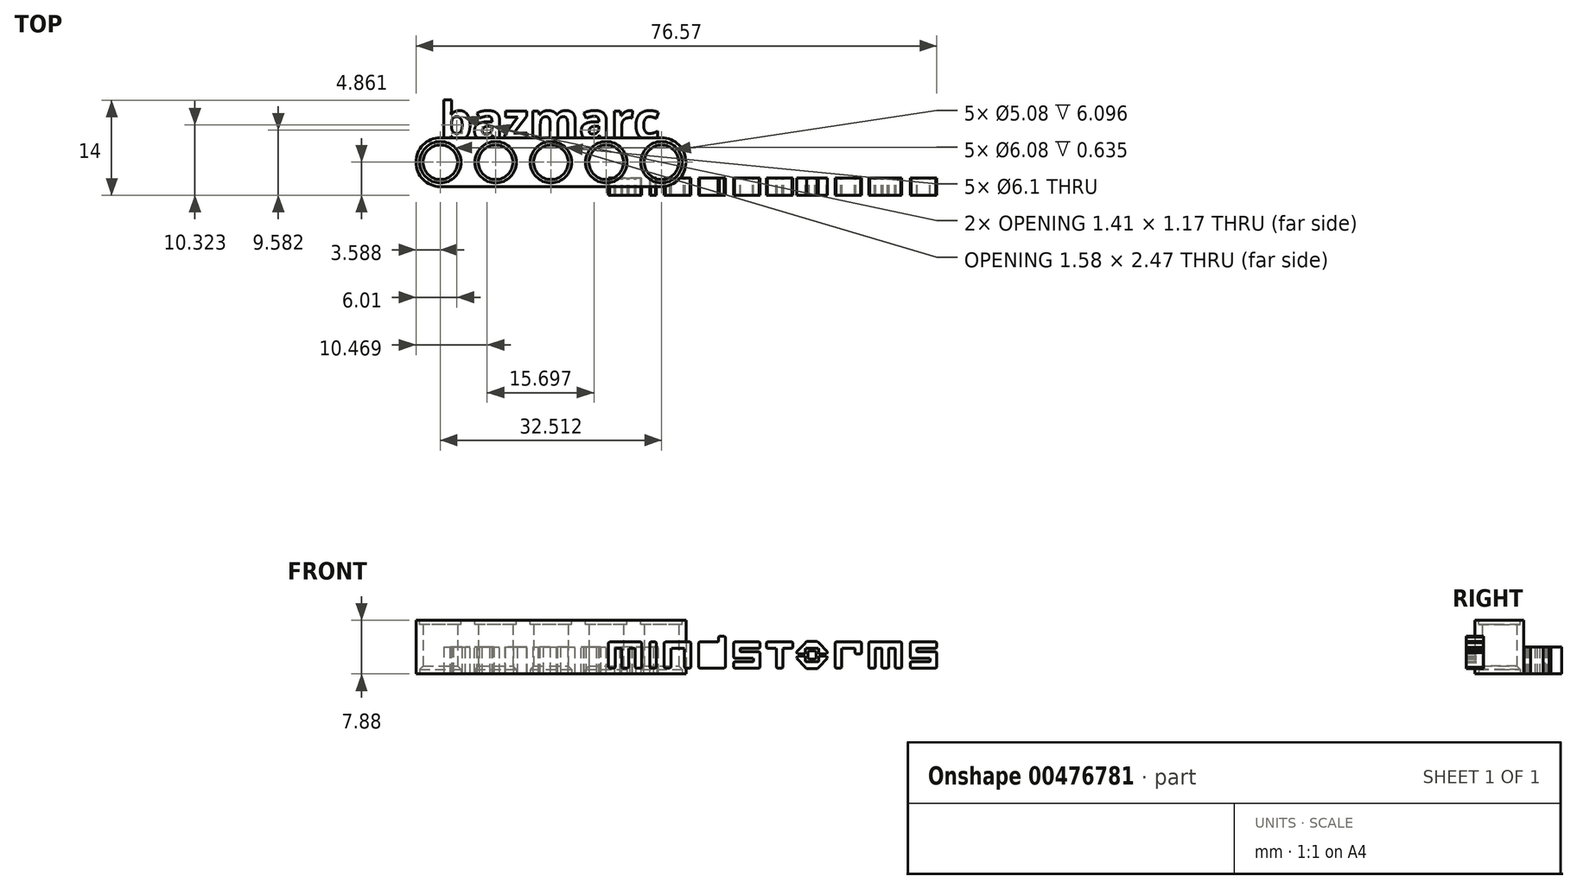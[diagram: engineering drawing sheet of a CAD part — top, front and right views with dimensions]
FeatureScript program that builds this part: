
annotation { "Feature Type Name" : "Feature", "Feature Type Description" : "" }
export const myFeature = defineFeature(function(context is Context, id is Id, definition is map)
    precondition{}
    {
        {
            var Q0;
            Q0=qCreatedBy(makeId("Top.planeOp"),FACE);
            var sketch = newSketch(context, id + "F0", { "sketchPlane" : qUnion([Q0])});
            skCircle(sketch, "E0", {"center": v(-60.84, 14.37) * mm, "radius": 3.6 * mm});
            skCircle(sketch, "E1.1.0.0", {"center": v(-52.71, 14.37) * mm, "radius": 3.6 * mm});
            skCircle(sketch, "E1.2.0.0", {"center": v(-44.59, 14.37) * mm, "radius": 3.6 * mm});
            skCircle(sketch, "E1.3.0.0", {"center": v(-36.46, 14.37) * mm, "radius": 3.6 * mm});
            skLineSegment(sketch, "E1.direction1", {"start": v(-60.84, 14.37) * mm, "end": v(-52.71, 14.37) * mm, "construction": true});
            skCircle(sketch, "E2.0.4.0", {"center": v(-28.33, 14.37) * mm, "radius": 3.6 * mm});
            skLineSegment(sketch, "E3.left", {"start": v(-60.84, 14.37) * mm, "end": v(-60.84, 14.37) * mm});
            skLineSegment(sketch, "E3.right", {"start": v(-28.33, 14.37) * mm, "end": v(-28.33, 14.37) * mm});
            skLineSegment(sketch, "E4.bottom", {"start": v(-60.84, 17.96) * mm, "end": v(-28.33, 17.96) * mm});
            skLineSegment(sketch, "E4.top", {"start": v(-60.84, 10.78) * mm, "end": v(-28.33, 10.78) * mm});
            skCircle(sketch, "E5", {"center": v(-60.84, 14.37) * mm, "radius": 3.05 * mm});
            skCircle(sketch, "E6.1.0.0", {"center": v(-52.71, 14.37) * mm, "radius": 3.05 * mm});
            skCircle(sketch, "E6.2.0.0", {"center": v(-44.59, 14.37) * mm, "radius": 3.05 * mm});
            skCircle(sketch, "E6.3.0.0", {"center": v(-36.46, 14.37) * mm, "radius": 3.05 * mm});
            skCircle(sketch, "E6.4.0.0", {"center": v(-28.33, 14.37) * mm, "radius": 3.05 * mm});
            skCircle(sketch, "E7", {"center": v(-60.84, 14.37) * mm, "radius": 2.54 * mm});
            skCircle(sketch, "E8.1.0.0", {"center": v(-52.71, 14.37) * mm, "radius": 2.54 * mm});
            skCircle(sketch, "E8.2.0.0", {"center": v(-44.59, 14.37) * mm, "radius": 2.54 * mm});
            skCircle(sketch, "E8.3.0.0", {"center": v(-36.46, 14.37) * mm, "radius": 2.54 * mm});
            skCircle(sketch, "E8.4.0.0", {"center": v(-28.33, 14.37) * mm, "radius": 2.54 * mm});
            skSolve(sketch);
        }
        {
            var Q0;
            Q0=makeQuery(id+"F0.imprint","IMPRINT",FACE,{"disambiguationData":[TD([[makeQuery(id+"F0.imprint","IMPRINT",EDGE,{"derivedFrom":sQuery(id+"F0.wireOp",EDGE,"E6.2.0.0")}),1.0]])]});
            var Q1;
            {var subQ0=sQuery(id+"F0.wireOp",EDGE,"E4.bottom");var subQ1=sQuery(id+"F0.wireOp",EDGE,"E0");var subQ2=makeQuery(id+"F0.imprint","INTERSECT",VERTEX,{"derivedFrom":[subQ1,subQ0]});Q1=makeQuery(id+"F0.imprint","IMPRINT",FACE,{"disambiguationData":[TD([[makeQuery(id+"F0.imprint","IMPRINT",EDGE,{"disambiguationData":[TD([[subQ2,1.0]])],"derivedFrom":subQ1}),-1.0]])]});}
            var Q2;
            {var subQ0=sQuery(id+"F0.wireOp",EDGE,"E4.bottom");var subQ1=sQuery(id+"F0.wireOp",EDGE,"E1.1.0.0");var subQ2=makeQuery(id+"F0.imprint","INTERSECT",VERTEX,{"derivedFrom":[subQ1,subQ0]});Q2=makeQuery(id+"F0.imprint","IMPRINT",FACE,{"disambiguationData":[TD([[makeQuery(id+"F0.imprint","IMPRINT",EDGE,{"disambiguationData":[TD([[subQ2,1.0]])],"derivedFrom":subQ1}),-1.0]])]});}
            var Q3;
            Q3=makeQuery(id+"F0.imprint","IMPRINT",FACE,{"disambiguationData":[TD([[makeQuery(id+"F0.imprint","IMPRINT",EDGE,{"derivedFrom":sQuery(id+"F0.wireOp",EDGE,"E6.2.0.0")}),-1.0]])]});
            var Q4;
            Q4=makeQuery(id+"F0.imprint","IMPRINT",FACE,{"disambiguationData":[TD([[makeQuery(id+"F0.imprint","IMPRINT",EDGE,{"derivedFrom":sQuery(id+"F0.wireOp",EDGE,"E6.1.0.0")}),-1.0]])]});
            var Q5;
            Q5=makeQuery(id+"F0.imprint","IMPRINT",FACE,{"disambiguationData":[TD([[makeQuery(id+"F0.imprint","IMPRINT",EDGE,{"derivedFrom":sQuery(id+"F0.wireOp",EDGE,"E6.3.0.0")}),-1.0]])]});
            var Q6;
            Q6=makeQuery(id+"F0.imprint","IMPRINT",FACE,{"disambiguationData":[TD([[makeQuery(id+"F0.imprint","IMPRINT",EDGE,{"derivedFrom":sQuery(id+"F0.wireOp",EDGE,"E6.3.0.0")}),1.0]])]});
            var Q7;
            {var subQ0=sQuery(id+"F0.wireOp",EDGE,"E4.bottom");var subQ1=sQuery(id+"F0.wireOp",EDGE,"E1.3.0.0");var subQ2=makeQuery(id+"F0.imprint","INTERSECT",VERTEX,{"derivedFrom":[subQ1,subQ0]});Q7=makeQuery(id+"F0.imprint","IMPRINT",FACE,{"disambiguationData":[TD([[makeQuery(id+"F0.imprint","IMPRINT",EDGE,{"disambiguationData":[TD([[subQ2,1.0]])],"derivedFrom":subQ1}),-1.0]])]});}
            var Q8;
            Q8=makeQuery(id+"F0.imprint","IMPRINT",FACE,{"disambiguationData":[TD([[makeQuery(id+"F0.imprint","IMPRINT",EDGE,{"derivedFrom":sQuery(id+"F0.wireOp",EDGE,"E6.4.0.0")}),-1.0]])]});
            var Q9;
            Q9=makeQuery(id+"F0.imprint","IMPRINT",FACE,{"disambiguationData":[TD([[makeQuery(id+"F0.imprint","IMPRINT",EDGE,{"derivedFrom":sQuery(id+"F0.wireOp",EDGE,"E6.1.0.0")}),1.0]])]});
            var Q10;
            {var subQ0=sQuery(id+"F0.wireOp",EDGE,"E4.bottom");var subQ1=sQuery(id+"F0.wireOp",EDGE,"E1.2.0.0");var subQ2=makeQuery(id+"F0.imprint","INTERSECT",VERTEX,{"derivedFrom":[subQ1,subQ0]});Q10=makeQuery(id+"F0.imprint","IMPRINT",FACE,{"disambiguationData":[TD([[makeQuery(id+"F0.imprint","IMPRINT",EDGE,{"disambiguationData":[TD([[subQ2,1.0]])],"derivedFrom":subQ1}),-1.0]])]});}
            var Q11;
            Q11=makeQuery(id+"F0.imprint","IMPRINT",FACE,{"disambiguationData":[TD([[makeQuery(id+"F0.imprint","IMPRINT",EDGE,{"derivedFrom":sQuery(id+"F0.wireOp",EDGE,"E6.4.0.0")}),1.0]])]});
            var Q12;
            Q12=makeQuery(id+"F0.imprint","IMPRINT",FACE,{"disambiguationData":[TD([[makeQuery(id+"F0.imprint","IMPRINT",EDGE,{"derivedFrom":sQuery(id+"F0.wireOp",EDGE,"E5")}),-1.0]])]});
            var Q13;
            Q13=makeQuery(id+"F0.imprint","IMPRINT",FACE,{"disambiguationData":[TD([[makeQuery(id+"F0.imprint","IMPRINT",EDGE,{"derivedFrom":sQuery(id+"F0.wireOp",EDGE,"E5")}),1.0]])]});
            extrude(context, id + "F1", {"entities" : qUnion([Q0, Q1, Q2, Q3, Q4, Q5, Q6, Q7, Q8, Q9, Q10, Q11, Q12, Q13]), "endBound" : BoundingType.SYMMETRIC, "depth" : 7.87 * mm});
        }
        {
            var Q0;
            Q0=makeQuery(id+"F1.opExtrude","CAP_FACE",FACE,{"disambiguationData":[OSD([sQuery(id+"F0.wireOp",EDGE,"E0"),sQuery(id+"F0.wireOp",EDGE,"E2.0.4.0"),sQuery(id+"F0.wireOp",EDGE,"E4.bottom"),sQuery(id+"F0.wireOp",EDGE,"E4.top"),sQuery(id+"F0.wireOp",EDGE,"E7"),sQuery(id+"F0.wireOp",EDGE,"E8.1.0.0"),sQuery(id+"F0.wireOp",EDGE,"E8.2.0.0"),sQuery(id+"F0.wireOp",EDGE,"E8.3.0.0"),sQuery(id+"F0.wireOp",EDGE,"E8.4.0.0")])],"isStart":false});
            var sketch = newSketch(context, id + "F2", { "sketchPlane" : qUnion([Q0])});
            skCircle(sketch, "E9", {"center": v(-28.33, 14.37) * mm, "radius": 3.04 * mm});
            skCircle(sketch, "E10.1.0.0", {"center": v(-36.46, 14.37) * mm, "radius": 3.04 * mm});
            skCircle(sketch, "E10.2.0.0", {"center": v(-44.59, 14.37) * mm, "radius": 3.04 * mm});
            skCircle(sketch, "E10.3.0.0", {"center": v(-52.71, 14.37) * mm, "radius": 3.04 * mm});
            skCircle(sketch, "E10.4.0.0", {"center": v(-60.84, 14.37) * mm, "radius": 3.04 * mm});
            skLineSegment(sketch, "E10.direction1", {"start": v(-28.33, 14.37) * mm, "end": v(-36.46, 14.37) * mm, "construction": true});
            skSolve(sketch);
        }
        {
            var Q0;
            Q0=qSketchRegion(id+"F2",true);
            extrude(context, id + "F3", {"entities" : qUnion([Q0]), "operationType" : NewBodyOperationType.REMOVE, "oppositeDirection" : true, "depth" : 0.64 * mm});
        }
        {
            var Q0;
            Q0=makeQuery(id+"F1.opExtrude","CAP_FACE",FACE,{"disambiguationData":[OSD([sQuery(id+"F0.wireOp",EDGE,"E0"),sQuery(id+"F0.wireOp",EDGE,"E2.0.4.0"),sQuery(id+"F0.wireOp",EDGE,"E4.bottom"),sQuery(id+"F0.wireOp",EDGE,"E4.top"),sQuery(id+"F0.wireOp",EDGE,"E7"),sQuery(id+"F0.wireOp",EDGE,"E8.1.0.0"),sQuery(id+"F0.wireOp",EDGE,"E8.2.0.0"),sQuery(id+"F0.wireOp",EDGE,"E8.3.0.0"),sQuery(id+"F0.wireOp",EDGE,"E8.4.0.0")])],"isStart":true});
            var sketch = newSketch(context, id + "F4", { "sketchPlane" : qUnion([Q0])});
            skCircle(sketch, "E11", {"center": v(-60.84, -14.37) * mm, "radius": 3.05 * mm});
            skCircle(sketch, "E12.1.0.0", {"center": v(-52.71, -14.37) * mm, "radius": 3.05 * mm});
            skCircle(sketch, "E12.2.0.0", {"center": v(-44.59, -14.37) * mm, "radius": 3.05 * mm});
            skCircle(sketch, "E12.3.0.0", {"center": v(-36.46, -14.37) * mm, "radius": 3.05 * mm});
            skCircle(sketch, "E12.4.0.0", {"center": v(-28.33, -14.37) * mm, "radius": 3.05 * mm});
            skLineSegment(sketch, "E12.direction1", {"start": v(-60.84, -14.37) * mm, "end": v(-52.71, -14.37) * mm, "construction": true});
            skSolve(sketch);
        }
        {
            var Q0;
            Q0=qSketchRegion(id+"F4",true);
            extrude(context, id + "F5", {"entities" : qUnion([Q0]), "operationType" : NewBodyOperationType.REMOVE, "oppositeDirection" : true, "depth" : 0.64 * mm});
        }
        {
            var Q0;
            Q0=qCreatedBy(makeId("Top.planeOp"),FACE);
            var sketch = newSketch(context, id + "F6", { "sketchPlane" : qUnion([Q0])});
            skText(sketch, "E13", { "text": "bazmarc", "fontName": "OpenSans-Bold.ttf"});
            const initialGuessF6  = {"E13": [-0.06093, 0.01776, 1, 0, 0.00545]};
            skSetInitialGuess(sketch, initialGuessF6);
            skSolve(sketch);
        }
        {
            var Q0;
            Q0=qSketchRegion(id+"F6",true);
            extrude(context, id + "F7", {"entities" : qUnion([Q0]), "operationType" : NewBodyOperationType.ADD, "oppositeDirection" : true, "depth" : 3.94 * mm});
        }
        {
            var Q0;
            Q0=makeQuery(id+"F5.boolean.opBoolean","INTERSECT",EDGE,{"derivedFrom":[makeQuery(id+"F1.opExtrude","SWEPT_FACE",FACE,{"disambiguationData":[OSD([sQuery(id+"F0.wireOp",EDGE,"E8.3.0.0")])]}),makeQuery(id+"F5.opExtrude","CAP_FACE",FACE,{"disambiguationData":[OSD([sQuery(id+"F4.wireOp",EDGE,"E12.3.0.0")])],"isStart":false})]});
            chamfer(context, id + "F8", {"entities" : qUnion([Q0]), "chamferType" : ChamferType.OFFSET_ANGLE, "width" : 0.5 * mm, "oppositeDirection" : false, "angle" : 45 * degree});
        }
        {
            var Q0;
            Q0=makeQuery(id+"F5.boolean.opBoolean","INTERSECT",EDGE,{"derivedFrom":[makeQuery(id+"F1.opExtrude","SWEPT_FACE",FACE,{"disambiguationData":[OSD([sQuery(id+"F0.wireOp",EDGE,"E8.2.0.0")])]}),makeQuery(id+"F5.opExtrude","CAP_FACE",FACE,{"disambiguationData":[OSD([sQuery(id+"F4.wireOp",EDGE,"E12.2.0.0")])],"isStart":false})]});
            var Q1;
            Q1=makeQuery(id+"F5.boolean.opBoolean","INTERSECT",EDGE,{"derivedFrom":[makeQuery(id+"F1.opExtrude","SWEPT_FACE",FACE,{"disambiguationData":[OSD([sQuery(id+"F0.wireOp",EDGE,"E8.1.0.0")])]}),makeQuery(id+"F5.opExtrude","CAP_FACE",FACE,{"disambiguationData":[OSD([sQuery(id+"F4.wireOp",EDGE,"E12.1.0.0")])],"isStart":false})]});
            var Q2;
            Q2=makeQuery(id+"F5.boolean.opBoolean","INTERSECT",EDGE,{"derivedFrom":[makeQuery(id+"F1.opExtrude","SWEPT_FACE",FACE,{"disambiguationData":[OSD([sQuery(id+"F0.wireOp",EDGE,"E7")])]}),makeQuery(id+"F5.opExtrude","CAP_FACE",FACE,{"disambiguationData":[OSD([sQuery(id+"F4.wireOp",EDGE,"E11")])],"isStart":false})]});
            var Q3;
            Q3=makeQuery(id+"F5.boolean.opBoolean","INTERSECT",EDGE,{"derivedFrom":[makeQuery(id+"F1.opExtrude","SWEPT_FACE",FACE,{"disambiguationData":[OSD([sQuery(id+"F0.wireOp",EDGE,"E8.4.0.0")])]}),makeQuery(id+"F5.opExtrude","CAP_FACE",FACE,{"disambiguationData":[OSD([sQuery(id+"F4.wireOp",EDGE,"E12.4.0.0")])],"isStart":false})]});
            chamfer(context, id + "F9", {"entities" : qUnion([Q0, Q1, Q2, Q3]), "chamferType" : ChamferType.OFFSET_ANGLE, "width" : 0.5 * mm, "oppositeDirection" : false, "angle" : 45 * degree});
        }
        {
            var Q0;
            Q0=makeQuery(id+"F1.opExtrude","SWEPT_FACE",FACE,{"disambiguationData":[OSD([sQuery(id+"F0.wireOp",EDGE,"E4.top")])]});
            var sketch = newSketch(context, id + "F10", { "sketchPlane" : qUnion([Q0])});
            skLineSegment(sketch, "E14", {"start": v(3.4, -0.27) * mm, "end": v(3.94, -0.27) * mm});
            skLineSegment(sketch, "E15", {"start": v(3.94, -0.27) * mm, "end": v(3.96, -0.27) * mm});
            skLineSegment(sketch, "E16", {"start": v(3.96, -0.27) * mm, "end": v(4.03, -0.42) * mm});
            skLineSegment(sketch, "E17", {"start": v(4.03, -0.42) * mm, "end": v(4.02, -0.43) * mm});
            skLineSegment(sketch, "E18", {"start": v(4.02, -0.43) * mm, "end": v(3.38, -1.1) * mm});
            skLineSegment(sketch, "E19", {"start": v(3.38, -1.1) * mm, "end": v(3.36, -1.13) * mm});
            skLineSegment(sketch, "E20", {"start": v(3.36, -1.13) * mm, "end": v(3.28, -1.2) * mm});
            skLineSegment(sketch, "E21", {"start": v(3.28, -1.2) * mm, "end": v(3.26, -1.2) * mm});
            skLineSegment(sketch, "E22", {"start": v(3.26, -1.2) * mm, "end": v(2.53, -1.2) * mm});
            skLineSegment(sketch, "E23", {"start": v(2.53, -1.2) * mm, "end": v(2.5, -1.2) * mm});
            skLineSegment(sketch, "E24", {"start": v(2.5, -1.2) * mm, "end": v(2.41, -1.12) * mm});
            skLineSegment(sketch, "E25", {"start": v(2.41, -1.12) * mm, "end": v(2.39, -1.09) * mm});
            skLineSegment(sketch, "E26", {"start": v(2.39, -1.09) * mm, "end": v(1.77, -0.43) * mm});
            skLineSegment(sketch, "E27", {"start": v(1.77, -0.43) * mm, "end": v(1.75, -0.42) * mm});
            skLineSegment(sketch, "E28", {"start": v(1.75, -0.42) * mm, "end": v(1.82, -0.27) * mm});
            skLineSegment(sketch, "E29", {"start": v(1.82, -0.27) * mm, "end": v(1.84, -0.27) * mm});
            skLineSegment(sketch, "E30", {"start": v(1.84, -0.27) * mm, "end": v(2.4, -0.27) * mm});
            skLineSegment(sketch, "E31", {"start": v(2.4, -0.27) * mm, "end": v(2.4, -0.64) * mm});
            skLineSegment(sketch, "E32", {"start": v(2.4, -0.64) * mm, "end": v(2.4, -0.64) * mm});
            skLineSegment(sketch, "E33", {"start": v(2.4, -0.64) * mm, "end": v(2.43, -0.68) * mm});
            skLineSegment(sketch, "E34", {"start": v(2.43, -0.68) * mm, "end": v(2.44, -0.68) * mm});
            skLineSegment(sketch, "E35", {"start": v(2.44, -0.68) * mm, "end": v(3.34, -0.68) * mm});
            skLineSegment(sketch, "E36", {"start": v(3.34, -0.68) * mm, "end": v(3.35, -0.68) * mm});
            skLineSegment(sketch, "E37", {"start": v(3.35, -0.68) * mm, "end": v(3.4, -0.65) * mm});
            skLineSegment(sketch, "E38", {"start": v(3.4, -0.65) * mm, "end": v(3.4, -0.64) * mm});
            skLineSegment(sketch, "E39", {"start": v(3.4, -0.64) * mm, "end": v(3.4, -0.27) * mm});
            skLineSegment(sketch, "E40", {"start": v(3.4, -0.12) * mm, "end": v(3.94, -0.12) * mm});
            skLineSegment(sketch, "E41", {"start": v(3.94, -0.12) * mm, "end": v(3.96, -0.12) * mm});
            skLineSegment(sketch, "E42", {"start": v(3.96, -0.12) * mm, "end": v(4.03, 0.03) * mm});
            skLineSegment(sketch, "E43", {"start": v(4.03, 0.03) * mm, "end": v(4.02, 0.04) * mm});
            skLineSegment(sketch, "E44", {"start": v(4.02, 0.04) * mm, "end": v(3.38, 0.7) * mm});
            skLineSegment(sketch, "E45", {"start": v(3.38, 0.7) * mm, "end": v(3.36, 0.73) * mm});
            skLineSegment(sketch, "E46", {"start": v(3.36, 0.73) * mm, "end": v(3.27, 0.8) * mm});
            skLineSegment(sketch, "E47", {"start": v(3.27, 0.8) * mm, "end": v(3.26, 0.8) * mm});
            skLineSegment(sketch, "E48", {"start": v(3.26, 0.8) * mm, "end": v(2.53, 0.8) * mm});
            skLineSegment(sketch, "E49", {"start": v(2.53, 0.8) * mm, "end": v(2.5, 0.8) * mm});
            skLineSegment(sketch, "E50", {"start": v(2.5, 0.8) * mm, "end": v(2.41, 0.72) * mm});
            skLineSegment(sketch, "E51", {"start": v(2.41, 0.72) * mm, "end": v(2.39, 0.7) * mm});
            skLineSegment(sketch, "E52", {"start": v(2.39, 0.7) * mm, "end": v(1.77, 0.04) * mm});
            skLineSegment(sketch, "E53", {"start": v(1.77, 0.04) * mm, "end": v(1.75, 0.03) * mm});
            skLineSegment(sketch, "E54", {"start": v(1.75, 0.03) * mm, "end": v(1.82, -0.12) * mm});
            skLineSegment(sketch, "E55", {"start": v(1.82, -0.12) * mm, "end": v(1.84, -0.12) * mm});
            skLineSegment(sketch, "E56", {"start": v(1.84, -0.12) * mm, "end": v(2.4, -0.12) * mm});
            skLineSegment(sketch, "E57", {"start": v(2.4, -0.12) * mm, "end": v(2.4, 0.24) * mm});
            skLineSegment(sketch, "E58", {"start": v(2.4, 0.24) * mm, "end": v(2.4, 0.25) * mm});
            skLineSegment(sketch, "E59", {"start": v(2.4, 0.25) * mm, "end": v(2.43, 0.29) * mm});
            skLineSegment(sketch, "E60", {"start": v(2.43, 0.29) * mm, "end": v(2.44, 0.29) * mm});
            skLineSegment(sketch, "E61", {"start": v(2.44, 0.29) * mm, "end": v(3.34, 0.29) * mm});
            skLineSegment(sketch, "E62", {"start": v(3.34, 0.29) * mm, "end": v(3.35, 0.29) * mm});
            skLineSegment(sketch, "E63", {"start": v(3.35, 0.29) * mm, "end": v(3.4, 0.25) * mm});
            skLineSegment(sketch, "E64", {"start": v(3.4, 0.25) * mm, "end": v(3.4, 0.24) * mm});
            skLineSegment(sketch, "E65", {"start": v(3.4, 0.24) * mm, "end": v(3.4, -0.12) * mm});
            skLineSegment(sketch, "E66", {"start": v(6.44, 0.78) * mm, "end": v(4.68, 0.78) * mm});
            skLineSegment(sketch, "E67", {"start": v(4.68, 0.78) * mm, "end": v(4.65, 0.78) * mm});
            skLineSegment(sketch, "E68", {"start": v(4.65, 0.78) * mm, "end": v(4.58, 0.7) * mm});
            skLineSegment(sketch, "E69", {"start": v(4.58, 0.7) * mm, "end": v(4.58, 0.68) * mm});
            skLineSegment(sketch, "E70", {"start": v(4.58, 0.68) * mm, "end": v(4.58, -1.08) * mm});
            skLineSegment(sketch, "E71", {"start": v(4.58, -1.08) * mm, "end": v(4.58, -1.1) * mm});
            skLineSegment(sketch, "E72", {"start": v(4.58, -1.1) * mm, "end": v(4.65, -1.17) * mm});
            skLineSegment(sketch, "E73", {"start": v(4.65, -1.17) * mm, "end": v(4.68, -1.17) * mm});
            skLineSegment(sketch, "E74", {"start": v(4.68, -1.17) * mm, "end": v(4.97, -1.17) * mm});
            skLineSegment(sketch, "E75", {"start": v(4.97, -1.17) * mm, "end": v(5, -1.17) * mm});
            skLineSegment(sketch, "E76", {"start": v(5, -1.17) * mm, "end": v(5.07, -1.1) * mm});
            skLineSegment(sketch, "E77", {"start": v(5.07, -1.1) * mm, "end": v(5.07, -1.08) * mm});
            skLineSegment(sketch, "E78", {"start": v(5.07, -1.08) * mm, "end": v(5.07, 0.24) * mm});
            skLineSegment(sketch, "E79", {"start": v(5.07, 0.24) * mm, "end": v(5.07, 0.25) * mm});
            skLineSegment(sketch, "E80", {"start": v(5.07, 0.25) * mm, "end": v(5.1, 0.29) * mm});
            skLineSegment(sketch, "E81", {"start": v(5.1, 0.29) * mm, "end": v(5.12, 0.29) * mm});
            skLineSegment(sketch, "E82", {"start": v(5.12, 0.29) * mm, "end": v(6, 0.29) * mm});
            skLineSegment(sketch, "E83", {"start": v(6, 0.29) * mm, "end": v(6, 0.29) * mm});
            skLineSegment(sketch, "E84", {"start": v(6, 0.29) * mm, "end": v(6.05, 0.25) * mm});
            skLineSegment(sketch, "E85", {"start": v(6.05, 0.25) * mm, "end": v(6.05, 0.24) * mm});
            skLineSegment(sketch, "E86", {"start": v(6.05, 0.24) * mm, "end": v(6.05, -0.02) * mm});
            skLineSegment(sketch, "E87", {"start": v(6.05, -0.02) * mm, "end": v(6.05, -0.04) * mm});
            skLineSegment(sketch, "E88", {"start": v(6.05, -0.04) * mm, "end": v(6.12, -0.12) * mm});
            skLineSegment(sketch, "E89", {"start": v(6.12, -0.12) * mm, "end": v(6.14, -0.12) * mm});
            skLineSegment(sketch, "E90", {"start": v(6.14, -0.12) * mm, "end": v(6.44, -0.12) * mm});
            skLineSegment(sketch, "E91", {"start": v(6.44, -0.12) * mm, "end": v(6.46, -0.12) * mm});
            skLineSegment(sketch, "E92", {"start": v(6.46, -0.12) * mm, "end": v(6.53, -0.04) * mm});
            skLineSegment(sketch, "E93", {"start": v(6.53, -0.04) * mm, "end": v(6.53, -0.02) * mm});
            skLineSegment(sketch, "E94", {"start": v(6.53, -0.02) * mm, "end": v(6.53, 0.68) * mm});
            skLineSegment(sketch, "E95", {"start": v(6.53, 0.68) * mm, "end": v(6.53, 0.7) * mm});
            skLineSegment(sketch, "E96", {"start": v(6.53, 0.7) * mm, "end": v(6.46, 0.78) * mm});
            skLineSegment(sketch, "E97", {"start": v(6.46, 0.78) * mm, "end": v(6.44, 0.78) * mm});
            skLineSegment(sketch, "E98", {"start": v(10.6, 0.24) * mm, "end": v(10.6, 0.25) * mm});
            skLineSegment(sketch, "E99", {"start": v(10.6, 0.25) * mm, "end": v(10.64, 0.29) * mm});
            skLineSegment(sketch, "E100", {"start": v(10.64, 0.29) * mm, "end": v(10.65, 0.29) * mm});
            skLineSegment(sketch, "E101", {"start": v(10.65, 0.29) * mm, "end": v(11.96, 0.29) * mm});
            skLineSegment(sketch, "E102", {"start": v(11.96, 0.29) * mm, "end": v(11.99, 0.29) * mm});
            skLineSegment(sketch, "E103", {"start": v(11.99, 0.29) * mm, "end": v(12.06, 0.36) * mm});
            skLineSegment(sketch, "E104", {"start": v(12.06, 0.36) * mm, "end": v(12.06, 0.39) * mm});
            skLineSegment(sketch, "E105", {"start": v(12.06, 0.39) * mm, "end": v(12.06, 0.68) * mm});
            skLineSegment(sketch, "E106", {"start": v(12.06, 0.68) * mm, "end": v(12.06, 0.7) * mm});
            skLineSegment(sketch, "E107", {"start": v(12.06, 0.7) * mm, "end": v(11.99, 0.78) * mm});
            skLineSegment(sketch, "E108", {"start": v(11.99, 0.78) * mm, "end": v(11.96, 0.78) * mm});
            skLineSegment(sketch, "E109", {"start": v(11.96, 0.78) * mm, "end": v(10.21, 0.78) * mm});
            skLineSegment(sketch, "E110", {"start": v(10.21, 0.78) * mm, "end": v(10.19, 0.78) * mm});
            skLineSegment(sketch, "E111", {"start": v(10.19, 0.78) * mm, "end": v(10.11, 0.7) * mm});
            skLineSegment(sketch, "E112", {"start": v(10.11, 0.7) * mm, "end": v(10.11, 0.68) * mm});
            skLineSegment(sketch, "E113", {"start": v(10.11, 0.68) * mm, "end": v(10.11, -0.35) * mm});
            skLineSegment(sketch, "E114", {"start": v(10.11, -0.35) * mm, "end": v(10.11, -0.37) * mm});
            skLineSegment(sketch, "E115", {"start": v(10.11, -0.37) * mm, "end": v(10.19, -0.44) * mm});
            skLineSegment(sketch, "E116", {"start": v(10.19, -0.44) * mm, "end": v(10.21, -0.44) * mm});
            skLineSegment(sketch, "E117", {"start": v(10.21, -0.44) * mm, "end": v(11.53, -0.44) * mm});
            skLineSegment(sketch, "E118", {"start": v(11.53, -0.44) * mm, "end": v(11.54, -0.44) * mm});
            skLineSegment(sketch, "E119", {"start": v(11.54, -0.44) * mm, "end": v(11.57, -0.48) * mm});
            skLineSegment(sketch, "E120", {"start": v(11.57, -0.48) * mm, "end": v(11.57, -0.49) * mm});
            skLineSegment(sketch, "E121", {"start": v(11.57, -0.49) * mm, "end": v(11.57, -0.64) * mm});
            skLineSegment(sketch, "E122", {"start": v(11.57, -0.64) * mm, "end": v(11.57, -0.65) * mm});
            skLineSegment(sketch, "E123", {"start": v(11.57, -0.65) * mm, "end": v(11.53, -0.68) * mm});
            skLineSegment(sketch, "E124", {"start": v(11.53, -0.68) * mm, "end": v(11.53, -0.68) * mm});
            skLineSegment(sketch, "E125", {"start": v(11.53, -0.68) * mm, "end": v(10.21, -0.68) * mm});
            skLineSegment(sketch, "E126", {"start": v(10.21, -0.68) * mm, "end": v(10.19, -0.68) * mm});
            skLineSegment(sketch, "E127", {"start": v(10.19, -0.68) * mm, "end": v(10.11, -0.76) * mm});
            skLineSegment(sketch, "E128", {"start": v(10.11, -0.76) * mm, "end": v(10.11, -0.78) * mm});
            skLineSegment(sketch, "E129", {"start": v(10.11, -0.78) * mm, "end": v(10.11, -1.08) * mm});
            skLineSegment(sketch, "E130", {"start": v(10.11, -1.08) * mm, "end": v(10.11, -1.1) * mm});
            skLineSegment(sketch, "E131", {"start": v(10.11, -1.1) * mm, "end": v(10.19, -1.17) * mm});
            skLineSegment(sketch, "E132", {"start": v(10.19, -1.17) * mm, "end": v(10.21, -1.17) * mm});
            skLineSegment(sketch, "E133", {"start": v(10.21, -1.17) * mm, "end": v(11.96, -1.17) * mm});
            skLineSegment(sketch, "E134", {"start": v(11.96, -1.17) * mm, "end": v(11.99, -1.17) * mm});
            skLineSegment(sketch, "E135", {"start": v(11.99, -1.17) * mm, "end": v(12.06, -1.1) * mm});
            skLineSegment(sketch, "E136", {"start": v(12.06, -1.1) * mm, "end": v(12.06, -1.08) * mm});
            skLineSegment(sketch, "E137", {"start": v(12.06, -1.08) * mm, "end": v(12.06, -0.05) * mm});
            skLineSegment(sketch, "E138", {"start": v(12.06, -0.05) * mm, "end": v(12.06, -0.03) * mm});
            skLineSegment(sketch, "E139", {"start": v(12.06, -0.03) * mm, "end": v(11.99, 0.04) * mm});
            skLineSegment(sketch, "E140", {"start": v(11.99, 0.04) * mm, "end": v(11.96, 0.04) * mm});
            skLineSegment(sketch, "E141", {"start": v(11.96, 0.04) * mm, "end": v(10.65, 0.04) * mm});
            skLineSegment(sketch, "E142", {"start": v(10.65, 0.04) * mm, "end": v(10.64, 0.04) * mm});
            skLineSegment(sketch, "E143", {"start": v(10.64, 0.04) * mm, "end": v(10.6, 0.08) * mm});
            skLineSegment(sketch, "E144", {"start": v(10.6, 0.08) * mm, "end": v(10.6, 0.1) * mm});
            skLineSegment(sketch, "E145", {"start": v(10.6, 0.1) * mm, "end": v(10.6, 0.24) * mm});
            skLineSegment(sketch, "E146", {"start": v(-2.4, 0.24) * mm, "end": v(-2.4, 0.25) * mm});
            skLineSegment(sketch, "E147", {"start": v(-2.4, 0.25) * mm, "end": v(-2.36, 0.29) * mm});
            skLineSegment(sketch, "E148", {"start": v(-2.36, 0.29) * mm, "end": v(-2.34, 0.29) * mm});
            skLineSegment(sketch, "E149", {"start": v(-2.34, 0.29) * mm, "end": v(-1.03, 0.29) * mm});
            skLineSegment(sketch, "E150", {"start": v(-1.03, 0.29) * mm, "end": v(-1, 0.29) * mm});
            skLineSegment(sketch, "E151", {"start": v(-1, 0.29) * mm, "end": v(-0.93, 0.36) * mm});
            skLineSegment(sketch, "E152", {"start": v(-0.93, 0.36) * mm, "end": v(-0.93, 0.39) * mm});
            skLineSegment(sketch, "E153", {"start": v(-0.93, 0.39) * mm, "end": v(-0.93, 0.68) * mm});
            skLineSegment(sketch, "E154", {"start": v(-0.93, 0.68) * mm, "end": v(-0.93, 0.7) * mm});
            skLineSegment(sketch, "E155", {"start": v(-0.93, 0.7) * mm, "end": v(-1, 0.78) * mm});
            skLineSegment(sketch, "E156", {"start": v(-1, 0.78) * mm, "end": v(-1.03, 0.78) * mm});
            skLineSegment(sketch, "E157", {"start": v(-1.03, 0.78) * mm, "end": v(-2.78, 0.78) * mm});
            skLineSegment(sketch, "E158", {"start": v(-2.78, 0.78) * mm, "end": v(-2.8, 0.78) * mm});
            skLineSegment(sketch, "E159", {"start": v(-2.8, 0.78) * mm, "end": v(-2.88, 0.7) * mm});
            skLineSegment(sketch, "E160", {"start": v(-2.88, 0.7) * mm, "end": v(-2.88, 0.68) * mm});
            skLineSegment(sketch, "E161", {"start": v(-2.88, 0.68) * mm, "end": v(-2.88, -0.35) * mm});
            skLineSegment(sketch, "E162", {"start": v(-2.88, -0.35) * mm, "end": v(-2.88, -0.37) * mm});
            skLineSegment(sketch, "E163", {"start": v(-2.88, -0.37) * mm, "end": v(-2.8, -0.44) * mm});
            skLineSegment(sketch, "E164", {"start": v(-2.8, -0.44) * mm, "end": v(-2.78, -0.44) * mm});
            skLineSegment(sketch, "E165", {"start": v(-2.78, -0.44) * mm, "end": v(-1.46, -0.44) * mm});
            skLineSegment(sketch, "E166", {"start": v(-1.46, -0.44) * mm, "end": v(-1.45, -0.44) * mm});
            skLineSegment(sketch, "E167", {"start": v(-1.45, -0.44) * mm, "end": v(-1.42, -0.48) * mm});
            skLineSegment(sketch, "E168", {"start": v(-1.42, -0.48) * mm, "end": v(-1.42, -0.49) * mm});
            skLineSegment(sketch, "E169", {"start": v(-1.42, -0.49) * mm, "end": v(-1.42, -0.64) * mm});
            skLineSegment(sketch, "E170", {"start": v(-1.42, -0.64) * mm, "end": v(-1.42, -0.65) * mm});
            skLineSegment(sketch, "E171", {"start": v(-1.42, -0.65) * mm, "end": v(-1.46, -0.68) * mm});
            skLineSegment(sketch, "E172", {"start": v(-1.46, -0.68) * mm, "end": v(-1.46, -0.68) * mm});
            skLineSegment(sketch, "E173", {"start": v(-1.46, -0.68) * mm, "end": v(-2.78, -0.68) * mm});
            skLineSegment(sketch, "E174", {"start": v(-2.78, -0.68) * mm, "end": v(-2.8, -0.68) * mm});
            skLineSegment(sketch, "E175", {"start": v(-2.8, -0.68) * mm, "end": v(-2.88, -0.76) * mm});
            skLineSegment(sketch, "E176", {"start": v(-2.88, -0.76) * mm, "end": v(-2.88, -0.78) * mm});
            skLineSegment(sketch, "E177", {"start": v(-2.88, -0.78) * mm, "end": v(-2.88, -1.08) * mm});
            skLineSegment(sketch, "E178", {"start": v(-2.88, -1.08) * mm, "end": v(-2.88, -1.1) * mm});
            skLineSegment(sketch, "E179", {"start": v(-2.88, -1.1) * mm, "end": v(-2.8, -1.17) * mm});
            skLineSegment(sketch, "E180", {"start": v(-2.8, -1.17) * mm, "end": v(-2.78, -1.17) * mm});
            skLineSegment(sketch, "E181", {"start": v(-2.78, -1.17) * mm, "end": v(-1.03, -1.17) * mm});
            skLineSegment(sketch, "E182", {"start": v(-1.03, -1.17) * mm, "end": v(-1, -1.17) * mm});
            skLineSegment(sketch, "E183", {"start": v(-1, -1.17) * mm, "end": v(-0.93, -1.1) * mm});
            skLineSegment(sketch, "E184", {"start": v(-0.93, -1.1) * mm, "end": v(-0.93, -1.08) * mm});
            skLineSegment(sketch, "E185", {"start": v(-0.93, -1.08) * mm, "end": v(-0.93, -0.05) * mm});
            skLineSegment(sketch, "E186", {"start": v(-0.93, -0.05) * mm, "end": v(-0.93, -0.03) * mm});
            skLineSegment(sketch, "E187", {"start": v(-0.93, -0.03) * mm, "end": v(-1, 0.04) * mm});
            skLineSegment(sketch, "E188", {"start": v(-1, 0.04) * mm, "end": v(-1.03, 0.04) * mm});
            skLineSegment(sketch, "E189", {"start": v(-1.03, 0.04) * mm, "end": v(-2.34, 0.04) * mm});
            skLineSegment(sketch, "E190", {"start": v(-2.34, 0.04) * mm, "end": v(-2.35, 0.04) * mm});
            skLineSegment(sketch, "E191", {"start": v(-2.35, 0.04) * mm, "end": v(-2.4, 0.08) * mm});
            skLineSegment(sketch, "E192", {"start": v(-2.4, 0.08) * mm, "end": v(-2.4, 0.1) * mm});
            skLineSegment(sketch, "E193", {"start": v(-2.4, 0.1) * mm, "end": v(-2.4, 0.24) * mm});
            skLineSegment(sketch, "E194", {"start": v(-3.98, -0.64) * mm, "end": v(-3.98, -0.65) * mm});
            skLineSegment(sketch, "E195", {"start": v(-3.98, -0.65) * mm, "end": v(-4.01, -0.68) * mm});
            skLineSegment(sketch, "E196", {"start": v(-4.01, -0.68) * mm, "end": v(-4.02, -0.68) * mm});
            skLineSegment(sketch, "E197", {"start": v(-4.02, -0.68) * mm, "end": v(-4.9, -0.68) * mm});
            skLineSegment(sketch, "E198", {"start": v(-4.9, -0.68) * mm, "end": v(-4.92, -0.68) * mm});
            skLineSegment(sketch, "E199", {"start": v(-4.92, -0.68) * mm, "end": v(-4.96, -0.65) * mm});
            skLineSegment(sketch, "E200", {"start": v(-4.96, -0.65) * mm, "end": v(-4.96, -0.64) * mm});
            skLineSegment(sketch, "E201", {"start": v(-4.96, -0.64) * mm, "end": v(-4.96, 0.24) * mm});
            skLineSegment(sketch, "E202", {"start": v(-4.96, 0.24) * mm, "end": v(-4.96, 0.25) * mm});
            skLineSegment(sketch, "E203", {"start": v(-4.96, 0.25) * mm, "end": v(-4.92, 0.29) * mm});
            skLineSegment(sketch, "E204", {"start": v(-4.92, 0.29) * mm, "end": v(-4.9, 0.29) * mm});
            skLineSegment(sketch, "E205", {"start": v(-4.9, 0.29) * mm, "end": v(-4.02, 0.29) * mm});
            skLineSegment(sketch, "E206", {"start": v(-4.02, 0.29) * mm, "end": v(-4.01, 0.29) * mm});
            skLineSegment(sketch, "E207", {"start": v(-4.01, 0.29) * mm, "end": v(-3.98, 0.25) * mm});
            skLineSegment(sketch, "E208", {"start": v(-3.98, 0.25) * mm, "end": v(-3.98, 0.24) * mm});
            skLineSegment(sketch, "E209", {"start": v(-3.98, 0.24) * mm, "end": v(-3.98, -0.64) * mm});
            skLineSegment(sketch, "E210", {"start": v(-3.59, 1.2) * mm, "end": v(-3.88, 1.2) * mm});
            skLineSegment(sketch, "E211", {"start": v(-3.88, 1.2) * mm, "end": v(-3.9, 1.2) * mm});
            skLineSegment(sketch, "E212", {"start": v(-3.9, 1.2) * mm, "end": v(-3.98, 1.12) * mm});
            skLineSegment(sketch, "E213", {"start": v(-3.98, 1.12) * mm, "end": v(-3.98, 1.1) * mm});
            skLineSegment(sketch, "E214", {"start": v(-3.98, 1.1) * mm, "end": v(-3.98, 0.82) * mm});
            skLineSegment(sketch, "E215", {"start": v(-3.98, 0.82) * mm, "end": v(-3.98, 0.81) * mm});
            skLineSegment(sketch, "E216", {"start": v(-3.98, 0.81) * mm, "end": v(-4.01, 0.78) * mm});
            skLineSegment(sketch, "E217", {"start": v(-4.01, 0.78) * mm, "end": v(-4.02, 0.78) * mm});
            skLineSegment(sketch, "E218", {"start": v(-4.02, 0.78) * mm, "end": v(-5.35, 0.78) * mm});
            skLineSegment(sketch, "E219", {"start": v(-5.35, 0.78) * mm, "end": v(-5.37, 0.78) * mm});
            skLineSegment(sketch, "E220", {"start": v(-5.37, 0.78) * mm, "end": v(-5.44, 0.7) * mm});
            skLineSegment(sketch, "E221", {"start": v(-5.44, 0.7) * mm, "end": v(-5.44, 0.68) * mm});
            skLineSegment(sketch, "E222", {"start": v(-5.44, 0.68) * mm, "end": v(-5.44, -1.08) * mm});
            skLineSegment(sketch, "E223", {"start": v(-5.44, -1.08) * mm, "end": v(-5.44, -1.1) * mm});
            skLineSegment(sketch, "E224", {"start": v(-5.44, -1.1) * mm, "end": v(-5.37, -1.17) * mm});
            skLineSegment(sketch, "E225", {"start": v(-5.37, -1.17) * mm, "end": v(-5.35, -1.17) * mm});
            skLineSegment(sketch, "E226", {"start": v(-5.35, -1.17) * mm, "end": v(-3.59, -1.17) * mm});
            skLineSegment(sketch, "E227", {"start": v(-3.59, -1.17) * mm, "end": v(-3.56, -1.17) * mm});
            skLineSegment(sketch, "E228", {"start": v(-3.56, -1.17) * mm, "end": v(-3.49, -1.1) * mm});
            skLineSegment(sketch, "E229", {"start": v(-3.49, -1.1) * mm, "end": v(-3.49, -1.08) * mm});
            skLineSegment(sketch, "E230", {"start": v(-3.49, -1.08) * mm, "end": v(-3.49, 1.1) * mm});
            skLineSegment(sketch, "E231", {"start": v(-3.49, 1.1) * mm, "end": v(-3.49, 1.12) * mm});
            skLineSegment(sketch, "E232", {"start": v(-3.49, 1.12) * mm, "end": v(-3.56, 1.2) * mm});
            skLineSegment(sketch, "E233", {"start": v(-3.56, 1.2) * mm, "end": v(-3.59, 1.2) * mm});
            skLineSegment(sketch, "E234", {"start": v(1.39, 0.78) * mm, "end": v(-0.36, 0.78) * mm});
            skLineSegment(sketch, "E235", {"start": v(-0.36, 0.78) * mm, "end": v(-0.39, 0.78) * mm});
            skLineSegment(sketch, "E236", {"start": v(-0.39, 0.78) * mm, "end": v(-0.46, 0.7) * mm});
            skLineSegment(sketch, "E237", {"start": v(-0.46, 0.7) * mm, "end": v(-0.46, 0.68) * mm});
            skLineSegment(sketch, "E238", {"start": v(-0.46, 0.68) * mm, "end": v(-0.46, 0.39) * mm});
            skLineSegment(sketch, "E239", {"start": v(-0.46, 0.39) * mm, "end": v(-0.46, 0.36) * mm});
            skLineSegment(sketch, "E240", {"start": v(-0.46, 0.36) * mm, "end": v(-0.39, 0.29) * mm});
            skLineSegment(sketch, "E241", {"start": v(-0.39, 0.29) * mm, "end": v(-0.36, 0.29) * mm});
            skLineSegment(sketch, "E242", {"start": v(-0.36, 0.29) * mm, "end": v(0.23, 0.29) * mm});
            skLineSegment(sketch, "E243", {"start": v(0.23, 0.29) * mm, "end": v(0.24, 0.29) * mm});
            skLineSegment(sketch, "E244", {"start": v(0.24, 0.29) * mm, "end": v(0.27, 0.25) * mm});
            skLineSegment(sketch, "E245", {"start": v(0.27, 0.25) * mm, "end": v(0.28, 0.24) * mm});
            skLineSegment(sketch, "E246", {"start": v(0.28, 0.24) * mm, "end": v(0.28, -1.08) * mm});
            skLineSegment(sketch, "E247", {"start": v(0.28, -1.08) * mm, "end": v(0.28, -1.1) * mm});
            skLineSegment(sketch, "E248", {"start": v(0.28, -1.1) * mm, "end": v(0.35, -1.17) * mm});
            skLineSegment(sketch, "E249", {"start": v(0.35, -1.17) * mm, "end": v(0.37, -1.17) * mm});
            skLineSegment(sketch, "E250", {"start": v(0.37, -1.17) * mm, "end": v(0.66, -1.17) * mm});
            skLineSegment(sketch, "E251", {"start": v(0.66, -1.17) * mm, "end": v(0.69, -1.17) * mm});
            skLineSegment(sketch, "E252", {"start": v(0.69, -1.17) * mm, "end": v(0.76, -1.1) * mm});
            skLineSegment(sketch, "E253", {"start": v(0.76, -1.1) * mm, "end": v(0.76, -1.08) * mm});
            skLineSegment(sketch, "E254", {"start": v(0.76, -1.08) * mm, "end": v(0.76, 0.24) * mm});
            skLineSegment(sketch, "E255", {"start": v(0.76, 0.24) * mm, "end": v(0.76, 0.25) * mm});
            skLineSegment(sketch, "E256", {"start": v(0.76, 0.25) * mm, "end": v(0.8, 0.29) * mm});
            skLineSegment(sketch, "E257", {"start": v(0.8, 0.29) * mm, "end": v(0.81, 0.29) * mm});
            skLineSegment(sketch, "E258", {"start": v(0.81, 0.29) * mm, "end": v(1.39, 0.29) * mm});
            skLineSegment(sketch, "E259", {"start": v(1.39, 0.29) * mm, "end": v(1.41, 0.29) * mm});
            skLineSegment(sketch, "E260", {"start": v(1.41, 0.29) * mm, "end": v(1.49, 0.36) * mm});
            skLineSegment(sketch, "E261", {"start": v(1.49, 0.36) * mm, "end": v(1.49, 0.39) * mm});
            skLineSegment(sketch, "E262", {"start": v(1.49, 0.39) * mm, "end": v(1.49, 0.68) * mm});
            skLineSegment(sketch, "E263", {"start": v(1.49, 0.68) * mm, "end": v(1.49, 0.7) * mm});
            skLineSegment(sketch, "E264", {"start": v(1.49, 0.7) * mm, "end": v(1.41, 0.78) * mm});
            skLineSegment(sketch, "E265", {"start": v(1.41, 0.78) * mm, "end": v(1.39, 0.78) * mm});
            skLineSegment(sketch, "E266", {"start": v(-6.12, 0.78) * mm, "end": v(-7.87, 0.78) * mm});
            skLineSegment(sketch, "E267", {"start": v(-7.87, 0.78) * mm, "end": v(-7.9, 0.78) * mm});
            skLineSegment(sketch, "E268", {"start": v(-7.9, 0.78) * mm, "end": v(-7.97, 0.7) * mm});
            skLineSegment(sketch, "E269", {"start": v(-7.97, 0.7) * mm, "end": v(-7.97, 0.68) * mm});
            skLineSegment(sketch, "E270", {"start": v(-7.97, 0.68) * mm, "end": v(-7.97, -1.08) * mm});
            skLineSegment(sketch, "E271", {"start": v(-7.97, -1.08) * mm, "end": v(-7.97, -1.1) * mm});
            skLineSegment(sketch, "E272", {"start": v(-7.97, -1.1) * mm, "end": v(-7.9, -1.17) * mm});
            skLineSegment(sketch, "E273", {"start": v(-7.9, -1.17) * mm, "end": v(-7.87, -1.17) * mm});
            skLineSegment(sketch, "E274", {"start": v(-7.87, -1.17) * mm, "end": v(-7.58, -1.17) * mm});
            skLineSegment(sketch, "E275", {"start": v(-7.58, -1.17) * mm, "end": v(-7.56, -1.17) * mm});
            skLineSegment(sketch, "E276", {"start": v(-7.56, -1.17) * mm, "end": v(-7.49, -1.1) * mm});
            skLineSegment(sketch, "E277", {"start": v(-7.49, -1.1) * mm, "end": v(-7.49, -1.08) * mm});
            skLineSegment(sketch, "E278", {"start": v(-7.49, -1.08) * mm, "end": v(-7.49, 0.24) * mm});
            skLineSegment(sketch, "E279", {"start": v(-7.49, 0.24) * mm, "end": v(-7.49, 0.25) * mm});
            skLineSegment(sketch, "E280", {"start": v(-7.49, 0.25) * mm, "end": v(-7.45, 0.29) * mm});
            skLineSegment(sketch, "E281", {"start": v(-7.45, 0.29) * mm, "end": v(-7.44, 0.29) * mm});
            skLineSegment(sketch, "E282", {"start": v(-7.44, 0.29) * mm, "end": v(-6.55, 0.29) * mm});
            skLineSegment(sketch, "E283", {"start": v(-6.55, 0.29) * mm, "end": v(-6.54, 0.29) * mm});
            skLineSegment(sketch, "E284", {"start": v(-6.54, 0.29) * mm, "end": v(-6.5, 0.25) * mm});
            skLineSegment(sketch, "E285", {"start": v(-6.5, 0.25) * mm, "end": v(-6.5, 0.24) * mm});
            skLineSegment(sketch, "E286", {"start": v(-6.5, 0.24) * mm, "end": v(-6.5, -1.08) * mm});
            skLineSegment(sketch, "E287", {"start": v(-6.5, -1.08) * mm, "end": v(-6.5, -1.1) * mm});
            skLineSegment(sketch, "E288", {"start": v(-6.5, -1.1) * mm, "end": v(-6.43, -1.17) * mm});
            skLineSegment(sketch, "E289", {"start": v(-6.43, -1.17) * mm, "end": v(-6.4, -1.17) * mm});
            skLineSegment(sketch, "E290", {"start": v(-6.4, -1.17) * mm, "end": v(-6.12, -1.17) * mm});
            skLineSegment(sketch, "E291", {"start": v(-6.12, -1.17) * mm, "end": v(-6.1, -1.17) * mm});
            skLineSegment(sketch, "E292", {"start": v(-6.1, -1.17) * mm, "end": v(-6.02, -1.1) * mm});
            skLineSegment(sketch, "E293", {"start": v(-6.02, -1.1) * mm, "end": v(-6.02, -1.08) * mm});
            skLineSegment(sketch, "E294", {"start": v(-6.02, -1.08) * mm, "end": v(-6.02, 0.68) * mm});
            skLineSegment(sketch, "E295", {"start": v(-6.02, 0.68) * mm, "end": v(-6.02, 0.7) * mm});
            skLineSegment(sketch, "E296", {"start": v(-6.02, 0.7) * mm, "end": v(-6.1, 0.78) * mm});
            skLineSegment(sketch, "E297", {"start": v(-6.1, 0.78) * mm, "end": v(-6.12, 0.78) * mm});
            skLineSegment(sketch, "E298", {"start": v(9.4, 0.78) * mm, "end": v(7.16, 0.78) * mm});
            skLineSegment(sketch, "E299", {"start": v(7.16, 0.78) * mm, "end": v(7.13, 0.78) * mm});
            skLineSegment(sketch, "E300", {"start": v(7.13, 0.78) * mm, "end": v(7.06, 0.7) * mm});
            skLineSegment(sketch, "E301", {"start": v(7.06, 0.7) * mm, "end": v(7.06, 0.68) * mm});
            skLineSegment(sketch, "E302", {"start": v(7.06, 0.68) * mm, "end": v(7.06, -1.08) * mm});
            skLineSegment(sketch, "E303", {"start": v(7.06, -1.08) * mm, "end": v(7.06, -1.1) * mm});
            skLineSegment(sketch, "E304", {"start": v(7.06, -1.1) * mm, "end": v(7.13, -1.17) * mm});
            skLineSegment(sketch, "E305", {"start": v(7.13, -1.17) * mm, "end": v(7.16, -1.17) * mm});
            skLineSegment(sketch, "E306", {"start": v(7.16, -1.17) * mm, "end": v(7.45, -1.17) * mm});
            skLineSegment(sketch, "E307", {"start": v(7.45, -1.17) * mm, "end": v(7.47, -1.17) * mm});
            skLineSegment(sketch, "E308", {"start": v(7.47, -1.17) * mm, "end": v(7.55, -1.1) * mm});
            skLineSegment(sketch, "E309", {"start": v(7.55, -1.1) * mm, "end": v(7.55, -1.08) * mm});
            skLineSegment(sketch, "E310", {"start": v(7.55, -1.08) * mm, "end": v(7.55, 0.24) * mm});
            skLineSegment(sketch, "E311", {"start": v(7.55, 0.24) * mm, "end": v(7.55, 0.25) * mm});
            skLineSegment(sketch, "E312", {"start": v(7.55, 0.25) * mm, "end": v(7.58, 0.29) * mm});
            skLineSegment(sketch, "E313", {"start": v(7.58, 0.29) * mm, "end": v(7.6, 0.29) * mm});
            skLineSegment(sketch, "E314", {"start": v(7.6, 0.29) * mm, "end": v(7.98, 0.29) * mm});
            skLineSegment(sketch, "E315", {"start": v(7.98, 0.29) * mm, "end": v(8, 0.29) * mm});
            skLineSegment(sketch, "E316", {"start": v(8, 0.29) * mm, "end": v(8.03, 0.25) * mm});
            skLineSegment(sketch, "E317", {"start": v(8.03, 0.25) * mm, "end": v(8.03, 0.24) * mm});
            skLineSegment(sketch, "E318", {"start": v(8.03, 0.24) * mm, "end": v(8.03, -1.08) * mm});
            skLineSegment(sketch, "E319", {"start": v(8.03, -1.08) * mm, "end": v(8.03, -1.1) * mm});
            skLineSegment(sketch, "E320", {"start": v(8.03, -1.1) * mm, "end": v(8.1, -1.17) * mm});
            skLineSegment(sketch, "E321", {"start": v(8.1, -1.17) * mm, "end": v(8.13, -1.17) * mm});
            skLineSegment(sketch, "E322", {"start": v(8.13, -1.17) * mm, "end": v(8.42, -1.17) * mm});
            skLineSegment(sketch, "E323", {"start": v(8.42, -1.17) * mm, "end": v(8.45, -1.17) * mm});
            skLineSegment(sketch, "E324", {"start": v(8.45, -1.17) * mm, "end": v(8.52, -1.1) * mm});
            skLineSegment(sketch, "E325", {"start": v(8.52, -1.1) * mm, "end": v(8.52, -1.08) * mm});
            skLineSegment(sketch, "E326", {"start": v(8.52, -1.08) * mm, "end": v(8.52, 0.24) * mm});
            skLineSegment(sketch, "E327", {"start": v(8.52, 0.24) * mm, "end": v(8.52, 0.25) * mm});
            skLineSegment(sketch, "E328", {"start": v(8.52, 0.25) * mm, "end": v(8.56, 0.29) * mm});
            skLineSegment(sketch, "E329", {"start": v(8.56, 0.29) * mm, "end": v(8.57, 0.29) * mm});
            skLineSegment(sketch, "E330", {"start": v(8.57, 0.29) * mm, "end": v(8.96, 0.29) * mm});
            skLineSegment(sketch, "E331", {"start": v(8.96, 0.29) * mm, "end": v(8.97, 0.29) * mm});
            skLineSegment(sketch, "E332", {"start": v(8.97, 0.29) * mm, "end": v(9, 0.25) * mm});
            skLineSegment(sketch, "E333", {"start": v(9, 0.25) * mm, "end": v(9, 0.24) * mm});
            skLineSegment(sketch, "E334", {"start": v(9, 0.24) * mm, "end": v(9, -1.08) * mm});
            skLineSegment(sketch, "E335", {"start": v(9, -1.08) * mm, "end": v(9, -1.1) * mm});
            skLineSegment(sketch, "E336", {"start": v(9, -1.1) * mm, "end": v(9.08, -1.17) * mm});
            skLineSegment(sketch, "E337", {"start": v(9.08, -1.17) * mm, "end": v(9.1, -1.17) * mm});
            skLineSegment(sketch, "E338", {"start": v(9.1, -1.17) * mm, "end": v(9.4, -1.17) * mm});
            skLineSegment(sketch, "E339", {"start": v(9.4, -1.17) * mm, "end": v(9.42, -1.17) * mm});
            skLineSegment(sketch, "E340", {"start": v(9.42, -1.17) * mm, "end": v(9.5, -1.1) * mm});
            skLineSegment(sketch, "E341", {"start": v(9.5, -1.1) * mm, "end": v(9.5, -1.08) * mm});
            skLineSegment(sketch, "E342", {"start": v(9.5, -1.08) * mm, "end": v(9.5, 0.68) * mm});
            skLineSegment(sketch, "E343", {"start": v(9.5, 0.68) * mm, "end": v(9.5, 0.7) * mm});
            skLineSegment(sketch, "E344", {"start": v(9.5, 0.7) * mm, "end": v(9.42, 0.78) * mm});
            skLineSegment(sketch, "E345", {"start": v(9.42, 0.78) * mm, "end": v(9.4, 0.78) * mm});
            skLineSegment(sketch, "E346", {"start": v(-9.72, 0.78) * mm, "end": v(-11.96, 0.78) * mm});
            skLineSegment(sketch, "E347", {"start": v(-11.96, 0.78) * mm, "end": v(-11.99, 0.78) * mm});
            skLineSegment(sketch, "E348", {"start": v(-11.99, 0.78) * mm, "end": v(-12.06, 0.7) * mm});
            skLineSegment(sketch, "E349", {"start": v(-12.06, 0.7) * mm, "end": v(-12.06, 0.68) * mm});
            skLineSegment(sketch, "E350", {"start": v(-12.06, 0.68) * mm, "end": v(-12.06, -1.08) * mm});
            skLineSegment(sketch, "E351", {"start": v(-12.06, -1.08) * mm, "end": v(-12.06, -1.1) * mm});
            skLineSegment(sketch, "E352", {"start": v(-12.06, -1.1) * mm, "end": v(-11.99, -1.17) * mm});
            skLineSegment(sketch, "E353", {"start": v(-11.99, -1.17) * mm, "end": v(-11.96, -1.17) * mm});
            skLineSegment(sketch, "E354", {"start": v(-11.96, -1.17) * mm, "end": v(-11.67, -1.17) * mm});
            skLineSegment(sketch, "E355", {"start": v(-11.67, -1.17) * mm, "end": v(-11.65, -1.17) * mm});
            skLineSegment(sketch, "E356", {"start": v(-11.65, -1.17) * mm, "end": v(-11.57, -1.1) * mm});
            skLineSegment(sketch, "E357", {"start": v(-11.57, -1.1) * mm, "end": v(-11.57, -1.08) * mm});
            skLineSegment(sketch, "E358", {"start": v(-11.57, -1.08) * mm, "end": v(-11.57, 0.24) * mm});
            skLineSegment(sketch, "E359", {"start": v(-11.57, 0.24) * mm, "end": v(-11.57, 0.25) * mm});
            skLineSegment(sketch, "E360", {"start": v(-11.57, 0.25) * mm, "end": v(-11.54, 0.29) * mm});
            skLineSegment(sketch, "E361", {"start": v(-11.54, 0.29) * mm, "end": v(-11.53, 0.29) * mm});
            skLineSegment(sketch, "E362", {"start": v(-11.53, 0.29) * mm, "end": v(-11.14, 0.29) * mm});
            skLineSegment(sketch, "E363", {"start": v(-11.14, 0.29) * mm, "end": v(-11.12, 0.29) * mm});
            skLineSegment(sketch, "E364", {"start": v(-11.12, 0.29) * mm, "end": v(-11.09, 0.25) * mm});
            skLineSegment(sketch, "E365", {"start": v(-11.09, 0.25) * mm, "end": v(-11.09, 0.24) * mm});
            skLineSegment(sketch, "E366", {"start": v(-11.09, 0.24) * mm, "end": v(-11.09, -1.08) * mm});
            skLineSegment(sketch, "E367", {"start": v(-11.09, -1.08) * mm, "end": v(-11.09, -1.1) * mm});
            skLineSegment(sketch, "E368", {"start": v(-11.09, -1.1) * mm, "end": v(-11.01, -1.17) * mm});
            skLineSegment(sketch, "E369", {"start": v(-11.01, -1.17) * mm, "end": v(-10.99, -1.17) * mm});
            skLineSegment(sketch, "E370", {"start": v(-10.99, -1.17) * mm, "end": v(-10.7, -1.17) * mm});
            skLineSegment(sketch, "E371", {"start": v(-10.7, -1.17) * mm, "end": v(-10.67, -1.17) * mm});
            skLineSegment(sketch, "E372", {"start": v(-10.67, -1.17) * mm, "end": v(-10.6, -1.1) * mm});
            skLineSegment(sketch, "E373", {"start": v(-10.6, -1.1) * mm, "end": v(-10.6, -1.08) * mm});
            skLineSegment(sketch, "E374", {"start": v(-10.6, -1.08) * mm, "end": v(-10.6, 0.24) * mm});
            skLineSegment(sketch, "E375", {"start": v(-10.6, 0.24) * mm, "end": v(-10.6, 0.25) * mm});
            skLineSegment(sketch, "E376", {"start": v(-10.6, 0.25) * mm, "end": v(-10.56, 0.29) * mm});
            skLineSegment(sketch, "E377", {"start": v(-10.56, 0.29) * mm, "end": v(-10.55, 0.29) * mm});
            skLineSegment(sketch, "E378", {"start": v(-10.55, 0.29) * mm, "end": v(-10.16, 0.29) * mm});
            skLineSegment(sketch, "E379", {"start": v(-10.16, 0.29) * mm, "end": v(-10.15, 0.29) * mm});
            skLineSegment(sketch, "E380", {"start": v(-10.15, 0.29) * mm, "end": v(-10.11, 0.25) * mm});
            skLineSegment(sketch, "E381", {"start": v(-10.11, 0.25) * mm, "end": v(-10.11, 0.24) * mm});
            skLineSegment(sketch, "E382", {"start": v(-10.11, 0.24) * mm, "end": v(-10.11, -1.08) * mm});
            skLineSegment(sketch, "E383", {"start": v(-10.11, -1.08) * mm, "end": v(-10.11, -1.1) * mm});
            skLineSegment(sketch, "E384", {"start": v(-10.11, -1.1) * mm, "end": v(-10.04, -1.17) * mm});
            skLineSegment(sketch, "E385", {"start": v(-10.04, -1.17) * mm, "end": v(-10.02, -1.17) * mm});
            skLineSegment(sketch, "E386", {"start": v(-10.02, -1.17) * mm, "end": v(-9.72, -1.17) * mm});
            skLineSegment(sketch, "E387", {"start": v(-9.72, -1.17) * mm, "end": v(-9.7, -1.17) * mm});
            skLineSegment(sketch, "E388", {"start": v(-9.7, -1.17) * mm, "end": v(-9.63, -1.1) * mm});
            skLineSegment(sketch, "E389", {"start": v(-9.63, -1.1) * mm, "end": v(-9.63, -1.08) * mm});
            skLineSegment(sketch, "E390", {"start": v(-9.63, -1.08) * mm, "end": v(-9.63, 0.68) * mm});
            skLineSegment(sketch, "E391", {"start": v(-9.63, 0.68) * mm, "end": v(-9.63, 0.7) * mm});
            skLineSegment(sketch, "E392", {"start": v(-9.63, 0.7) * mm, "end": v(-9.7, 0.78) * mm});
            skLineSegment(sketch, "E393", {"start": v(-9.7, 0.78) * mm, "end": v(-9.72, 0.78) * mm});
            skLineSegment(sketch, "E394", {"start": v(-8.56, -1.08) * mm, "end": v(-8.56, -1.1) * mm});
            skLineSegment(sketch, "E395", {"start": v(-8.56, -1.1) * mm, "end": v(-8.63, -1.17) * mm});
            skLineSegment(sketch, "E396", {"start": v(-8.63, -1.17) * mm, "end": v(-8.65, -1.17) * mm});
            skLineSegment(sketch, "E397", {"start": v(-8.65, -1.17) * mm, "end": v(-8.95, -1.17) * mm});
            skLineSegment(sketch, "E398", {"start": v(-8.95, -1.17) * mm, "end": v(-8.97, -1.17) * mm});
            skLineSegment(sketch, "E399", {"start": v(-8.97, -1.17) * mm, "end": v(-9.04, -1.1) * mm});
            skLineSegment(sketch, "E400", {"start": v(-9.04, -1.1) * mm, "end": v(-9.04, -1.08) * mm});
            skLineSegment(sketch, "E401", {"start": v(-9.04, -1.08) * mm, "end": v(-9.04, 0.68) * mm});
            skLineSegment(sketch, "E402", {"start": v(-9.04, 0.68) * mm, "end": v(-9.04, 0.7) * mm});
            skLineSegment(sketch, "E403", {"start": v(-9.04, 0.7) * mm, "end": v(-8.97, 0.78) * mm});
            skLineSegment(sketch, "E404", {"start": v(-8.97, 0.78) * mm, "end": v(-8.95, 0.78) * mm});
            skLineSegment(sketch, "E405", {"start": v(-8.95, 0.78) * mm, "end": v(-8.65, 0.78) * mm});
            skLineSegment(sketch, "E406", {"start": v(-8.65, 0.78) * mm, "end": v(-8.63, 0.78) * mm});
            skLineSegment(sketch, "E407", {"start": v(-8.63, 0.78) * mm, "end": v(-8.56, 0.7) * mm});
            skLineSegment(sketch, "E408", {"start": v(-8.56, 0.7) * mm, "end": v(-8.56, 0.68) * mm});
            skLineSegment(sketch, "E409", {"start": v(-8.56, 0.68) * mm, "end": v(-8.56, -1.08) * mm});
            skLineSegment(sketch, "E410", {"start": v(2.7, 0.1) * mm, "end": v(3.08, 0.1) * mm});
            skLineSegment(sketch, "E411", {"start": v(3.08, 0.1) * mm, "end": v(3.1, 0.1) * mm});
            skLineSegment(sketch, "E412", {"start": v(3.1, 0.1) * mm, "end": v(3.18, 0.02) * mm});
            skLineSegment(sketch, "E413", {"start": v(3.18, 0.02) * mm, "end": v(3.18, 0) * mm});
            skLineSegment(sketch, "E414", {"start": v(3.18, 0) * mm, "end": v(3.18, -0.39) * mm});
            skLineSegment(sketch, "E415", {"start": v(3.18, -0.39) * mm, "end": v(3.18, -0.4) * mm});
            skLineSegment(sketch, "E416", {"start": v(3.18, -0.4) * mm, "end": v(3.1, -0.48) * mm});
            skLineSegment(sketch, "E417", {"start": v(3.1, -0.48) * mm, "end": v(3.08, -0.48) * mm});
            skLineSegment(sketch, "E418", {"start": v(3.08, -0.48) * mm, "end": v(2.7, -0.48) * mm});
            skLineSegment(sketch, "E419", {"start": v(2.7, -0.48) * mm, "end": v(2.67, -0.48) * mm});
            skLineSegment(sketch, "E420", {"start": v(2.67, -0.48) * mm, "end": v(2.6, -0.4) * mm});
            skLineSegment(sketch, "E421", {"start": v(2.6, -0.4) * mm, "end": v(2.6, -0.39) * mm});
            skLineSegment(sketch, "E422", {"start": v(2.6, -0.39) * mm, "end": v(2.6, 0) * mm});
            skLineSegment(sketch, "E423", {"start": v(2.6, 0) * mm, "end": v(2.6, 0.02) * mm});
            skLineSegment(sketch, "E424", {"start": v(2.6, 0.02) * mm, "end": v(2.67, 0.1) * mm});
            skLineSegment(sketch, "E425", {"start": v(2.67, 0.1) * mm, "end": v(2.7, 0.1) * mm});
            skSolve(sketch);
        }
        {
            var Q0;
            Q0=makeQuery(id+"F10.imprint","IMPRINT",FACE,{"disambiguationData":[TD([[makeQuery(id+"F10.imprint","IMPRINT",EDGE,{"derivedFrom":sQuery(id+"F10.wireOp",EDGE,"E66")}),1.0]])]});
            var Q1;
            Q1=makeQuery(id+"F10.imprint","IMPRINT",FACE,{"disambiguationData":[TD([[makeQuery(id+"F10.imprint","IMPRINT",EDGE,{"derivedFrom":sQuery(id+"F10.wireOp",EDGE,"E346")}),1.0]])]});
            var Q2;
            Q2=makeQuery(id+"F10.imprint","IMPRINT",FACE,{"disambiguationData":[TD([[makeQuery(id+"F10.imprint","IMPRINT",EDGE,{"derivedFrom":sQuery(id+"F10.wireOp",EDGE,"E266")}),1.0]])]});
            var Q3;
            Q3=makeQuery(id+"F10.imprint","IMPRINT",FACE,{"disambiguationData":[TD([[makeQuery(id+"F10.imprint","IMPRINT",EDGE,{"derivedFrom":sQuery(id+"F10.wireOp",EDGE,"E194")}),1.0]])]});
            var Q4;
            Q4=makeQuery(id+"F10.imprint","IMPRINT",FACE,{"disambiguationData":[TD([[makeQuery(id+"F10.imprint","IMPRINT",EDGE,{"derivedFrom":sQuery(id+"F10.wireOp",EDGE,"E98")}),1.0]])]});
            var Q5;
            Q5=makeQuery(id+"F10.imprint","IMPRINT",FACE,{"disambiguationData":[TD([[makeQuery(id+"F10.imprint","IMPRINT",EDGE,{"derivedFrom":sQuery(id+"F10.wireOp",EDGE,"E146")}),1.0]])]});
            var Q6;
            Q6=makeQuery(id+"F10.imprint","IMPRINT",FACE,{"disambiguationData":[TD([[makeQuery(id+"F10.imprint","IMPRINT",EDGE,{"derivedFrom":sQuery(id+"F10.wireOp",EDGE,"E234")}),1.0]])]});
            var Q7;
            Q7=makeQuery(id+"F10.imprint","IMPRINT",FACE,{"disambiguationData":[TD([[makeQuery(id+"F10.imprint","IMPRINT",EDGE,{"derivedFrom":sQuery(id+"F10.wireOp",EDGE,"E194")}),-1.0]])]});
            var Q8;
            Q8=makeQuery(id+"F10.imprint","IMPRINT",FACE,{"disambiguationData":[TD([[makeQuery(id+"F10.imprint","IMPRINT",EDGE,{"derivedFrom":sQuery(id+"F10.wireOp",EDGE,"E298")}),1.0]])]});
            var Q9;
            Q9=makeQuery(id+"F10.imprint","IMPRINT",FACE,{"disambiguationData":[TD([[makeQuery(id+"F10.imprint","IMPRINT",EDGE,{"derivedFrom":sQuery(id+"F10.wireOp",EDGE,"E394")}),-1.0]])]});
            var Q10;
            Q10=makeQuery(id+"F10.imprint","IMPRINT",FACE,{"disambiguationData":[TD([[makeQuery(id+"F10.imprint","IMPRINT",EDGE,{"derivedFrom":sQuery(id+"F10.wireOp",EDGE,"E14")}),-1.0]])]});
            var Q11;
            Q11=makeQuery(id+"F10.imprint","IMPRINT",FACE,{"disambiguationData":[TD([[makeQuery(id+"F10.imprint","IMPRINT",EDGE,{"derivedFrom":sQuery(id+"F10.wireOp",EDGE,"E40")}),1.0]])]});
            var Q12;
            Q12=makeQuery(id+"F10.imprint","IMPRINT",FACE,{"disambiguationData":[TD([[makeQuery(id+"F10.imprint","IMPRINT",EDGE,{"derivedFrom":sQuery(id+"F10.wireOp",EDGE,"E410")}),-1.0]])]});
            extrude(context, id + "F11", {"entities" : qUnion([Q0, Q1, Q2, Q3, Q4, Q5, Q6, Q7, Q8, Q9, Q10, Q11, Q12]), "depth" : 1.27 * mm});
        }
        {
            var Q0;
            Q0=makeQuery(id+"F11.opExtrude","SWEPT_BODY",BODY,{"disambiguationData":[OSD([sQuery(id+"F10.wireOp",EDGE,"E40"),sQuery(id+"F10.wireOp",EDGE,"E41"),sQuery(id+"F10.wireOp",EDGE,"E42"),sQuery(id+"F10.wireOp",EDGE,"E43"),sQuery(id+"F10.wireOp",EDGE,"E44"),sQuery(id+"F10.wireOp",EDGE,"E45"),sQuery(id+"F10.wireOp",EDGE,"E46"),sQuery(id+"F10.wireOp",EDGE,"E47"),sQuery(id+"F10.wireOp",EDGE,"E48"),sQuery(id+"F10.wireOp",EDGE,"E49"),sQuery(id+"F10.wireOp",EDGE,"E50"),sQuery(id+"F10.wireOp",EDGE,"E51"),sQuery(id+"F10.wireOp",EDGE,"E52"),sQuery(id+"F10.wireOp",EDGE,"E53"),sQuery(id+"F10.wireOp",EDGE,"E54"),sQuery(id+"F10.wireOp",EDGE,"E55"),sQuery(id+"F10.wireOp",EDGE,"E56"),sQuery(id+"F10.wireOp",EDGE,"E57"),sQuery(id+"F10.wireOp",EDGE,"E58"),sQuery(id+"F10.wireOp",EDGE,"E59"),sQuery(id+"F10.wireOp",EDGE,"E60"),sQuery(id+"F10.wireOp",EDGE,"E61"),sQuery(id+"F10.wireOp",EDGE,"E62"),sQuery(id+"F10.wireOp",EDGE,"E63"),sQuery(id+"F10.wireOp",EDGE,"E64"),sQuery(id+"F10.wireOp",EDGE,"E65")])]});
            var Q1;
            Q1=makeQuery(id+"F11.opExtrude","SWEPT_BODY",BODY,{"disambiguationData":[OSD([sQuery(id+"F10.wireOp",EDGE,"E66"),sQuery(id+"F10.wireOp",EDGE,"E67"),sQuery(id+"F10.wireOp",EDGE,"E68"),sQuery(id+"F10.wireOp",EDGE,"E69"),sQuery(id+"F10.wireOp",EDGE,"E70"),sQuery(id+"F10.wireOp",EDGE,"E71"),sQuery(id+"F10.wireOp",EDGE,"E72"),sQuery(id+"F10.wireOp",EDGE,"E73"),sQuery(id+"F10.wireOp",EDGE,"E74"),sQuery(id+"F10.wireOp",EDGE,"E75"),sQuery(id+"F10.wireOp",EDGE,"E76"),sQuery(id+"F10.wireOp",EDGE,"E77"),sQuery(id+"F10.wireOp",EDGE,"E78"),sQuery(id+"F10.wireOp",EDGE,"E79"),sQuery(id+"F10.wireOp",EDGE,"E80"),sQuery(id+"F10.wireOp",EDGE,"E81"),sQuery(id+"F10.wireOp",EDGE,"E82"),sQuery(id+"F10.wireOp",EDGE,"E83"),sQuery(id+"F10.wireOp",EDGE,"E84"),sQuery(id+"F10.wireOp",EDGE,"E85"),sQuery(id+"F10.wireOp",EDGE,"E86"),sQuery(id+"F10.wireOp",EDGE,"E87"),sQuery(id+"F10.wireOp",EDGE,"E88"),sQuery(id+"F10.wireOp",EDGE,"E89"),sQuery(id+"F10.wireOp",EDGE,"E90"),sQuery(id+"F10.wireOp",EDGE,"E91"),sQuery(id+"F10.wireOp",EDGE,"E92"),sQuery(id+"F10.wireOp",EDGE,"E93"),sQuery(id+"F10.wireOp",EDGE,"E94"),sQuery(id+"F10.wireOp",EDGE,"E95"),sQuery(id+"F10.wireOp",EDGE,"E96"),sQuery(id+"F10.wireOp",EDGE,"E97")])]});
            var Q2;
            Q2=makeQuery(id+"F11.opExtrude","SWEPT_BODY",BODY,{"disambiguationData":[OSD([sQuery(id+"F10.wireOp",EDGE,"E98"),sQuery(id+"F10.wireOp",EDGE,"E99"),sQuery(id+"F10.wireOp",EDGE,"E100"),sQuery(id+"F10.wireOp",EDGE,"E101"),sQuery(id+"F10.wireOp",EDGE,"E102"),sQuery(id+"F10.wireOp",EDGE,"E103"),sQuery(id+"F10.wireOp",EDGE,"E104"),sQuery(id+"F10.wireOp",EDGE,"E105"),sQuery(id+"F10.wireOp",EDGE,"E106"),sQuery(id+"F10.wireOp",EDGE,"E107"),sQuery(id+"F10.wireOp",EDGE,"E108"),sQuery(id+"F10.wireOp",EDGE,"E109"),sQuery(id+"F10.wireOp",EDGE,"E110"),sQuery(id+"F10.wireOp",EDGE,"E111"),sQuery(id+"F10.wireOp",EDGE,"E112"),sQuery(id+"F10.wireOp",EDGE,"E113"),sQuery(id+"F10.wireOp",EDGE,"E114"),sQuery(id+"F10.wireOp",EDGE,"E115"),sQuery(id+"F10.wireOp",EDGE,"E116"),sQuery(id+"F10.wireOp",EDGE,"E117"),sQuery(id+"F10.wireOp",EDGE,"E118"),sQuery(id+"F10.wireOp",EDGE,"E119"),sQuery(id+"F10.wireOp",EDGE,"E120"),sQuery(id+"F10.wireOp",EDGE,"E121"),sQuery(id+"F10.wireOp",EDGE,"E122"),sQuery(id+"F10.wireOp",EDGE,"E123"),sQuery(id+"F10.wireOp",EDGE,"E124"),sQuery(id+"F10.wireOp",EDGE,"E125"),sQuery(id+"F10.wireOp",EDGE,"E126"),sQuery(id+"F10.wireOp",EDGE,"E127"),sQuery(id+"F10.wireOp",EDGE,"E128"),sQuery(id+"F10.wireOp",EDGE,"E129"),sQuery(id+"F10.wireOp",EDGE,"E130"),sQuery(id+"F10.wireOp",EDGE,"E131"),sQuery(id+"F10.wireOp",EDGE,"E132"),sQuery(id+"F10.wireOp",EDGE,"E133"),sQuery(id+"F10.wireOp",EDGE,"E134"),sQuery(id+"F10.wireOp",EDGE,"E135"),sQuery(id+"F10.wireOp",EDGE,"E136"),sQuery(id+"F10.wireOp",EDGE,"E137"),sQuery(id+"F10.wireOp",EDGE,"E138"),sQuery(id+"F10.wireOp",EDGE,"E139"),sQuery(id+"F10.wireOp",EDGE,"E140"),sQuery(id+"F10.wireOp",EDGE,"E141"),sQuery(id+"F10.wireOp",EDGE,"E142"),sQuery(id+"F10.wireOp",EDGE,"E143"),sQuery(id+"F10.wireOp",EDGE,"E144"),sQuery(id+"F10.wireOp",EDGE,"E145")])]});
            var Q3;
            Q3=makeQuery(id+"F11.opExtrude","SWEPT_BODY",BODY,{"disambiguationData":[OSD([sQuery(id+"F10.wireOp",EDGE,"E146"),sQuery(id+"F10.wireOp",EDGE,"E147"),sQuery(id+"F10.wireOp",EDGE,"E148"),sQuery(id+"F10.wireOp",EDGE,"E149"),sQuery(id+"F10.wireOp",EDGE,"E150"),sQuery(id+"F10.wireOp",EDGE,"E151"),sQuery(id+"F10.wireOp",EDGE,"E152"),sQuery(id+"F10.wireOp",EDGE,"E153"),sQuery(id+"F10.wireOp",EDGE,"E154"),sQuery(id+"F10.wireOp",EDGE,"E155"),sQuery(id+"F10.wireOp",EDGE,"E156"),sQuery(id+"F10.wireOp",EDGE,"E157"),sQuery(id+"F10.wireOp",EDGE,"E158"),sQuery(id+"F10.wireOp",EDGE,"E159"),sQuery(id+"F10.wireOp",EDGE,"E160"),sQuery(id+"F10.wireOp",EDGE,"E161"),sQuery(id+"F10.wireOp",EDGE,"E162"),sQuery(id+"F10.wireOp",EDGE,"E163"),sQuery(id+"F10.wireOp",EDGE,"E164"),sQuery(id+"F10.wireOp",EDGE,"E165"),sQuery(id+"F10.wireOp",EDGE,"E166"),sQuery(id+"F10.wireOp",EDGE,"E167"),sQuery(id+"F10.wireOp",EDGE,"E168"),sQuery(id+"F10.wireOp",EDGE,"E169"),sQuery(id+"F10.wireOp",EDGE,"E170"),sQuery(id+"F10.wireOp",EDGE,"E171"),sQuery(id+"F10.wireOp",EDGE,"E172"),sQuery(id+"F10.wireOp",EDGE,"E173"),sQuery(id+"F10.wireOp",EDGE,"E174"),sQuery(id+"F10.wireOp",EDGE,"E175"),sQuery(id+"F10.wireOp",EDGE,"E176"),sQuery(id+"F10.wireOp",EDGE,"E177"),sQuery(id+"F10.wireOp",EDGE,"E178"),sQuery(id+"F10.wireOp",EDGE,"E179"),sQuery(id+"F10.wireOp",EDGE,"E180"),sQuery(id+"F10.wireOp",EDGE,"E181"),sQuery(id+"F10.wireOp",EDGE,"E182"),sQuery(id+"F10.wireOp",EDGE,"E183"),sQuery(id+"F10.wireOp",EDGE,"E184"),sQuery(id+"F10.wireOp",EDGE,"E185"),sQuery(id+"F10.wireOp",EDGE,"E186"),sQuery(id+"F10.wireOp",EDGE,"E187"),sQuery(id+"F10.wireOp",EDGE,"E188"),sQuery(id+"F10.wireOp",EDGE,"E189"),sQuery(id+"F10.wireOp",EDGE,"E190"),sQuery(id+"F10.wireOp",EDGE,"E191"),sQuery(id+"F10.wireOp",EDGE,"E192"),sQuery(id+"F10.wireOp",EDGE,"E193")])]});
            var Q4;
            Q4=makeQuery(id+"F11.opExtrude","SWEPT_BODY",BODY,{"disambiguationData":[OSD([sQuery(id+"F10.wireOp",EDGE,"E210"),sQuery(id+"F10.wireOp",EDGE,"E211"),sQuery(id+"F10.wireOp",EDGE,"E212"),sQuery(id+"F10.wireOp",EDGE,"E213"),sQuery(id+"F10.wireOp",EDGE,"E214"),sQuery(id+"F10.wireOp",EDGE,"E215"),sQuery(id+"F10.wireOp",EDGE,"E216"),sQuery(id+"F10.wireOp",EDGE,"E217"),sQuery(id+"F10.wireOp",EDGE,"E218"),sQuery(id+"F10.wireOp",EDGE,"E219"),sQuery(id+"F10.wireOp",EDGE,"E220"),sQuery(id+"F10.wireOp",EDGE,"E221"),sQuery(id+"F10.wireOp",EDGE,"E222"),sQuery(id+"F10.wireOp",EDGE,"E223"),sQuery(id+"F10.wireOp",EDGE,"E224"),sQuery(id+"F10.wireOp",EDGE,"E225"),sQuery(id+"F10.wireOp",EDGE,"E226"),sQuery(id+"F10.wireOp",EDGE,"E227"),sQuery(id+"F10.wireOp",EDGE,"E228"),sQuery(id+"F10.wireOp",EDGE,"E229"),sQuery(id+"F10.wireOp",EDGE,"E230"),sQuery(id+"F10.wireOp",EDGE,"E231"),sQuery(id+"F10.wireOp",EDGE,"E232"),sQuery(id+"F10.wireOp",EDGE,"E233")])]});
            var Q5;
            Q5=makeQuery(id+"F11.opExtrude","SWEPT_BODY",BODY,{"disambiguationData":[OSD([sQuery(id+"F10.wireOp",EDGE,"E234"),sQuery(id+"F10.wireOp",EDGE,"E235"),sQuery(id+"F10.wireOp",EDGE,"E236"),sQuery(id+"F10.wireOp",EDGE,"E237"),sQuery(id+"F10.wireOp",EDGE,"E238"),sQuery(id+"F10.wireOp",EDGE,"E239"),sQuery(id+"F10.wireOp",EDGE,"E240"),sQuery(id+"F10.wireOp",EDGE,"E241"),sQuery(id+"F10.wireOp",EDGE,"E242"),sQuery(id+"F10.wireOp",EDGE,"E243"),sQuery(id+"F10.wireOp",EDGE,"E244"),sQuery(id+"F10.wireOp",EDGE,"E245"),sQuery(id+"F10.wireOp",EDGE,"E246"),sQuery(id+"F10.wireOp",EDGE,"E247"),sQuery(id+"F10.wireOp",EDGE,"E248"),sQuery(id+"F10.wireOp",EDGE,"E249"),sQuery(id+"F10.wireOp",EDGE,"E250"),sQuery(id+"F10.wireOp",EDGE,"E251"),sQuery(id+"F10.wireOp",EDGE,"E252"),sQuery(id+"F10.wireOp",EDGE,"E253"),sQuery(id+"F10.wireOp",EDGE,"E254"),sQuery(id+"F10.wireOp",EDGE,"E255"),sQuery(id+"F10.wireOp",EDGE,"E256"),sQuery(id+"F10.wireOp",EDGE,"E257"),sQuery(id+"F10.wireOp",EDGE,"E258"),sQuery(id+"F10.wireOp",EDGE,"E259"),sQuery(id+"F10.wireOp",EDGE,"E260"),sQuery(id+"F10.wireOp",EDGE,"E261"),sQuery(id+"F10.wireOp",EDGE,"E262"),sQuery(id+"F10.wireOp",EDGE,"E263"),sQuery(id+"F10.wireOp",EDGE,"E264"),sQuery(id+"F10.wireOp",EDGE,"E265")])]});
            var Q6;
            Q6=makeQuery(id+"F11.opExtrude","SWEPT_BODY",BODY,{"disambiguationData":[OSD([sQuery(id+"F10.wireOp",EDGE,"E266"),sQuery(id+"F10.wireOp",EDGE,"E267"),sQuery(id+"F10.wireOp",EDGE,"E268"),sQuery(id+"F10.wireOp",EDGE,"E269"),sQuery(id+"F10.wireOp",EDGE,"E270"),sQuery(id+"F10.wireOp",EDGE,"E271"),sQuery(id+"F10.wireOp",EDGE,"E272"),sQuery(id+"F10.wireOp",EDGE,"E273"),sQuery(id+"F10.wireOp",EDGE,"E274"),sQuery(id+"F10.wireOp",EDGE,"E275"),sQuery(id+"F10.wireOp",EDGE,"E276"),sQuery(id+"F10.wireOp",EDGE,"E277"),sQuery(id+"F10.wireOp",EDGE,"E278"),sQuery(id+"F10.wireOp",EDGE,"E279"),sQuery(id+"F10.wireOp",EDGE,"E280"),sQuery(id+"F10.wireOp",EDGE,"E281"),sQuery(id+"F10.wireOp",EDGE,"E282"),sQuery(id+"F10.wireOp",EDGE,"E283"),sQuery(id+"F10.wireOp",EDGE,"E284"),sQuery(id+"F10.wireOp",EDGE,"E285"),sQuery(id+"F10.wireOp",EDGE,"E286"),sQuery(id+"F10.wireOp",EDGE,"E287"),sQuery(id+"F10.wireOp",EDGE,"E288"),sQuery(id+"F10.wireOp",EDGE,"E289"),sQuery(id+"F10.wireOp",EDGE,"E290"),sQuery(id+"F10.wireOp",EDGE,"E291"),sQuery(id+"F10.wireOp",EDGE,"E292"),sQuery(id+"F10.wireOp",EDGE,"E293"),sQuery(id+"F10.wireOp",EDGE,"E294"),sQuery(id+"F10.wireOp",EDGE,"E295"),sQuery(id+"F10.wireOp",EDGE,"E296"),sQuery(id+"F10.wireOp",EDGE,"E297")])]});
            var Q7;
            Q7=makeQuery(id+"F11.opExtrude","SWEPT_BODY",BODY,{"disambiguationData":[OSD([sQuery(id+"F10.wireOp",EDGE,"E298"),sQuery(id+"F10.wireOp",EDGE,"E299"),sQuery(id+"F10.wireOp",EDGE,"E300"),sQuery(id+"F10.wireOp",EDGE,"E301"),sQuery(id+"F10.wireOp",EDGE,"E302"),sQuery(id+"F10.wireOp",EDGE,"E303"),sQuery(id+"F10.wireOp",EDGE,"E304"),sQuery(id+"F10.wireOp",EDGE,"E305"),sQuery(id+"F10.wireOp",EDGE,"E306"),sQuery(id+"F10.wireOp",EDGE,"E307"),sQuery(id+"F10.wireOp",EDGE,"E308"),sQuery(id+"F10.wireOp",EDGE,"E309"),sQuery(id+"F10.wireOp",EDGE,"E310"),sQuery(id+"F10.wireOp",EDGE,"E311"),sQuery(id+"F10.wireOp",EDGE,"E312"),sQuery(id+"F10.wireOp",EDGE,"E313"),sQuery(id+"F10.wireOp",EDGE,"E314"),sQuery(id+"F10.wireOp",EDGE,"E315"),sQuery(id+"F10.wireOp",EDGE,"E316"),sQuery(id+"F10.wireOp",EDGE,"E317"),sQuery(id+"F10.wireOp",EDGE,"E318"),sQuery(id+"F10.wireOp",EDGE,"E319"),sQuery(id+"F10.wireOp",EDGE,"E320"),sQuery(id+"F10.wireOp",EDGE,"E321"),sQuery(id+"F10.wireOp",EDGE,"E322"),sQuery(id+"F10.wireOp",EDGE,"E323"),sQuery(id+"F10.wireOp",EDGE,"E324"),sQuery(id+"F10.wireOp",EDGE,"E325"),sQuery(id+"F10.wireOp",EDGE,"E326"),sQuery(id+"F10.wireOp",EDGE,"E327"),sQuery(id+"F10.wireOp",EDGE,"E328"),sQuery(id+"F10.wireOp",EDGE,"E329"),sQuery(id+"F10.wireOp",EDGE,"E330"),sQuery(id+"F10.wireOp",EDGE,"E331"),sQuery(id+"F10.wireOp",EDGE,"E332"),sQuery(id+"F10.wireOp",EDGE,"E333"),sQuery(id+"F10.wireOp",EDGE,"E334"),sQuery(id+"F10.wireOp",EDGE,"E335"),sQuery(id+"F10.wireOp",EDGE,"E336"),sQuery(id+"F10.wireOp",EDGE,"E337"),sQuery(id+"F10.wireOp",EDGE,"E338"),sQuery(id+"F10.wireOp",EDGE,"E339"),sQuery(id+"F10.wireOp",EDGE,"E340"),sQuery(id+"F10.wireOp",EDGE,"E341"),sQuery(id+"F10.wireOp",EDGE,"E342"),sQuery(id+"F10.wireOp",EDGE,"E343"),sQuery(id+"F10.wireOp",EDGE,"E344"),sQuery(id+"F10.wireOp",EDGE,"E345")])]});
            var Q8;
            Q8=makeQuery(id+"F11.opExtrude","SWEPT_BODY",BODY,{"disambiguationData":[OSD([sQuery(id+"F10.wireOp",EDGE,"E346"),sQuery(id+"F10.wireOp",EDGE,"E347"),sQuery(id+"F10.wireOp",EDGE,"E348"),sQuery(id+"F10.wireOp",EDGE,"E349"),sQuery(id+"F10.wireOp",EDGE,"E350"),sQuery(id+"F10.wireOp",EDGE,"E351"),sQuery(id+"F10.wireOp",EDGE,"E352"),sQuery(id+"F10.wireOp",EDGE,"E353"),sQuery(id+"F10.wireOp",EDGE,"E354"),sQuery(id+"F10.wireOp",EDGE,"E355"),sQuery(id+"F10.wireOp",EDGE,"E356"),sQuery(id+"F10.wireOp",EDGE,"E357"),sQuery(id+"F10.wireOp",EDGE,"E358"),sQuery(id+"F10.wireOp",EDGE,"E359"),sQuery(id+"F10.wireOp",EDGE,"E360"),sQuery(id+"F10.wireOp",EDGE,"E361"),sQuery(id+"F10.wireOp",EDGE,"E362"),sQuery(id+"F10.wireOp",EDGE,"E363"),sQuery(id+"F10.wireOp",EDGE,"E364"),sQuery(id+"F10.wireOp",EDGE,"E365"),sQuery(id+"F10.wireOp",EDGE,"E366"),sQuery(id+"F10.wireOp",EDGE,"E367"),sQuery(id+"F10.wireOp",EDGE,"E368"),sQuery(id+"F10.wireOp",EDGE,"E369"),sQuery(id+"F10.wireOp",EDGE,"E370"),sQuery(id+"F10.wireOp",EDGE,"E371"),sQuery(id+"F10.wireOp",EDGE,"E372"),sQuery(id+"F10.wireOp",EDGE,"E373"),sQuery(id+"F10.wireOp",EDGE,"E374"),sQuery(id+"F10.wireOp",EDGE,"E375"),sQuery(id+"F10.wireOp",EDGE,"E376"),sQuery(id+"F10.wireOp",EDGE,"E377"),sQuery(id+"F10.wireOp",EDGE,"E378"),sQuery(id+"F10.wireOp",EDGE,"E379"),sQuery(id+"F10.wireOp",EDGE,"E380"),sQuery(id+"F10.wireOp",EDGE,"E381"),sQuery(id+"F10.wireOp",EDGE,"E382"),sQuery(id+"F10.wireOp",EDGE,"E383"),sQuery(id+"F10.wireOp",EDGE,"E384"),sQuery(id+"F10.wireOp",EDGE,"E385"),sQuery(id+"F10.wireOp",EDGE,"E386"),sQuery(id+"F10.wireOp",EDGE,"E387"),sQuery(id+"F10.wireOp",EDGE,"E388"),sQuery(id+"F10.wireOp",EDGE,"E389"),sQuery(id+"F10.wireOp",EDGE,"E390"),sQuery(id+"F10.wireOp",EDGE,"E391"),sQuery(id+"F10.wireOp",EDGE,"E392"),sQuery(id+"F10.wireOp",EDGE,"E393")])]});
            var Q9;
            Q9=makeQuery(id+"F11.opExtrude","SWEPT_BODY",BODY,{"disambiguationData":[OSD([sQuery(id+"F10.wireOp",EDGE,"E394"),sQuery(id+"F10.wireOp",EDGE,"E395"),sQuery(id+"F10.wireOp",EDGE,"E396"),sQuery(id+"F10.wireOp",EDGE,"E397"),sQuery(id+"F10.wireOp",EDGE,"E398"),sQuery(id+"F10.wireOp",EDGE,"E399"),sQuery(id+"F10.wireOp",EDGE,"E400"),sQuery(id+"F10.wireOp",EDGE,"E401"),sQuery(id+"F10.wireOp",EDGE,"E402"),sQuery(id+"F10.wireOp",EDGE,"E403"),sQuery(id+"F10.wireOp",EDGE,"E404"),sQuery(id+"F10.wireOp",EDGE,"E405"),sQuery(id+"F10.wireOp",EDGE,"E406"),sQuery(id+"F10.wireOp",EDGE,"E407"),sQuery(id+"F10.wireOp",EDGE,"E408"),sQuery(id+"F10.wireOp",EDGE,"E409")])]});
            var Q10;
            Q10=makeQuery(id+"F11.opExtrude","SWEPT_BODY",BODY,{"disambiguationData":[OSD([sQuery(id+"F10.wireOp",EDGE,"E14"),sQuery(id+"F10.wireOp",EDGE,"E15"),sQuery(id+"F10.wireOp",EDGE,"E16"),sQuery(id+"F10.wireOp",EDGE,"E17"),sQuery(id+"F10.wireOp",EDGE,"E18"),sQuery(id+"F10.wireOp",EDGE,"E19"),sQuery(id+"F10.wireOp",EDGE,"E20"),sQuery(id+"F10.wireOp",EDGE,"E21"),sQuery(id+"F10.wireOp",EDGE,"E22"),sQuery(id+"F10.wireOp",EDGE,"E23"),sQuery(id+"F10.wireOp",EDGE,"E24"),sQuery(id+"F10.wireOp",EDGE,"E25"),sQuery(id+"F10.wireOp",EDGE,"E26"),sQuery(id+"F10.wireOp",EDGE,"E27"),sQuery(id+"F10.wireOp",EDGE,"E28"),sQuery(id+"F10.wireOp",EDGE,"E29"),sQuery(id+"F10.wireOp",EDGE,"E30"),sQuery(id+"F10.wireOp",EDGE,"E31"),sQuery(id+"F10.wireOp",EDGE,"E32"),sQuery(id+"F10.wireOp",EDGE,"E33"),sQuery(id+"F10.wireOp",EDGE,"E34"),sQuery(id+"F10.wireOp",EDGE,"E35"),sQuery(id+"F10.wireOp",EDGE,"E36"),sQuery(id+"F10.wireOp",EDGE,"E37"),sQuery(id+"F10.wireOp",EDGE,"E38"),sQuery(id+"F10.wireOp",EDGE,"E39")])]});
            var Q11;
            Q11=makeQuery(id+"F11.opExtrude","SWEPT_BODY",BODY,{"disambiguationData":[OSD([sQuery(id+"F10.wireOp",EDGE,"E410"),sQuery(id+"F10.wireOp",EDGE,"E411"),sQuery(id+"F10.wireOp",EDGE,"E412"),sQuery(id+"F10.wireOp",EDGE,"E413"),sQuery(id+"F10.wireOp",EDGE,"E414"),sQuery(id+"F10.wireOp",EDGE,"E415"),sQuery(id+"F10.wireOp",EDGE,"E416"),sQuery(id+"F10.wireOp",EDGE,"E417"),sQuery(id+"F10.wireOp",EDGE,"E418"),sQuery(id+"F10.wireOp",EDGE,"E419"),sQuery(id+"F10.wireOp",EDGE,"E420"),sQuery(id+"F10.wireOp",EDGE,"E421"),sQuery(id+"F10.wireOp",EDGE,"E422"),sQuery(id+"F10.wireOp",EDGE,"E423"),sQuery(id+"F10.wireOp",EDGE,"E424"),sQuery(id+"F10.wireOp",EDGE,"E425")])]});
            var Q12;
            Q12=makeQuery(id+"F11.opExtrude","CAP_VERTEX",VERTEX,{"disambiguationData":[OSD([sQuery(id+"F10.wireOp",EDGE,"E107"),sQuery(id+"F10.wireOp",EDGE,"E108")])],"isStart":false});
            transform(context, id + "F12", {"entities" : qUnion([Q0, Q1, Q2, Q3, Q4, Q5, Q6, Q7, Q8, Q9, Q10, Q11]), "transformType" : TransformType.SCALE_UNIFORMLY, "scale" : 2, "scalePoint" : qUnion([Q12]), "makeCopy" : false});
        }
    });
